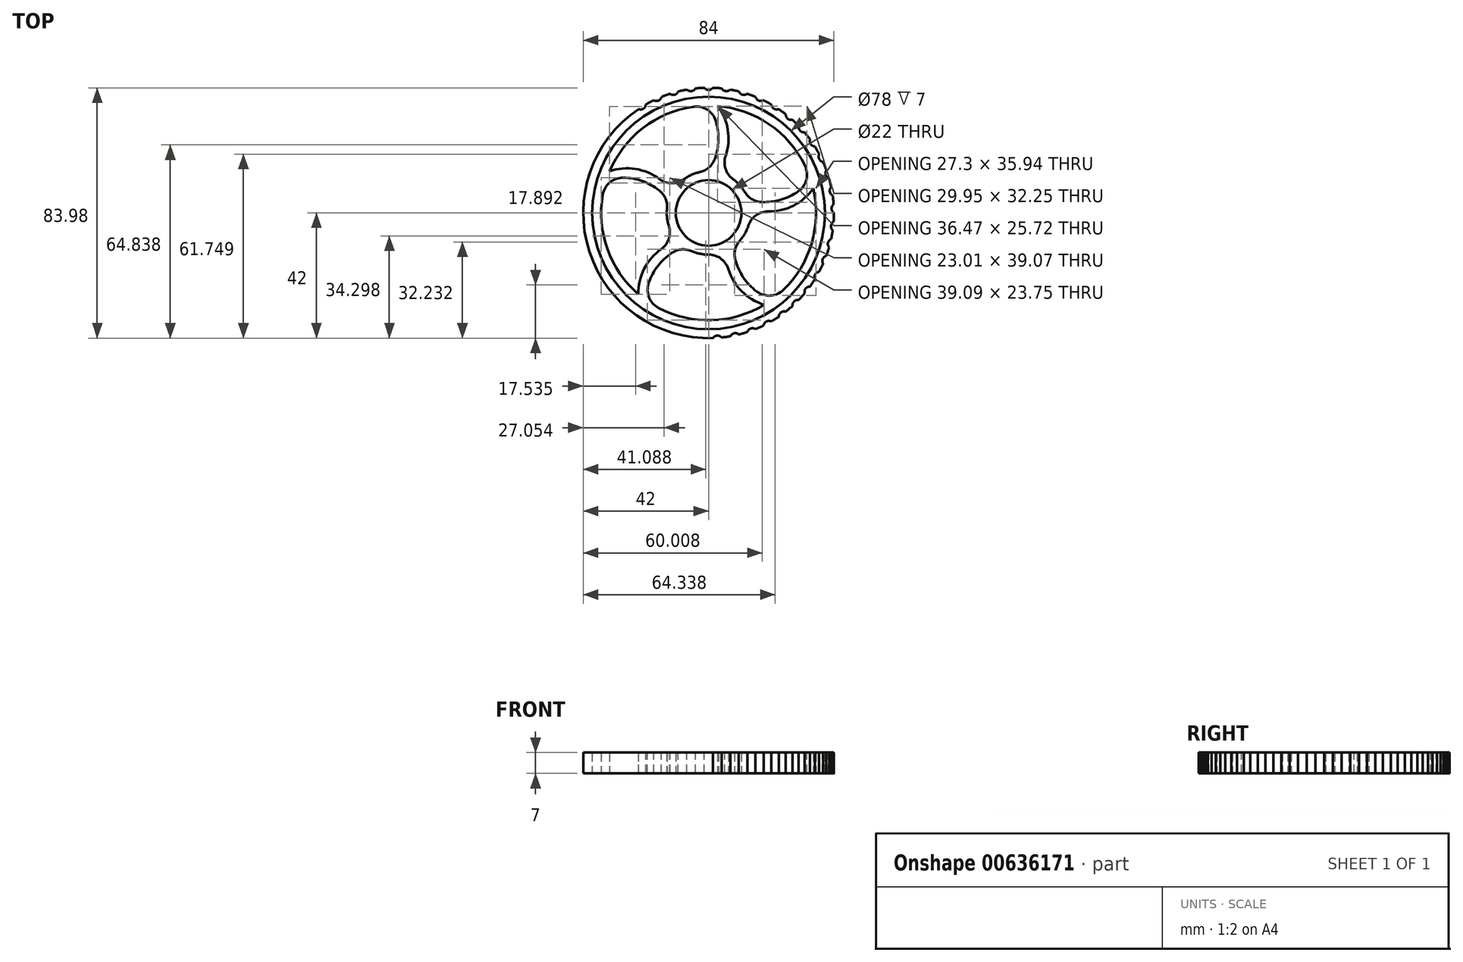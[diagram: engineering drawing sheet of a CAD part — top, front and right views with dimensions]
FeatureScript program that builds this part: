
annotation { "Feature Type Name" : "Feature", "Feature Type Description" : "" }
export const myFeature = defineFeature(function(context is Context, id is Id, definition is map)
    precondition{}
    {
        {
            var Q0;
            Q0=qCreatedBy(makeId("Top.planeOp"),FACE);
            var sketch = newSketch(context, id + "F0", { "sketchPlane" : qUnion([Q0])});
            skCircle(sketch, "E0", {"center": v(0, 0) * mm, "radius": 11 * mm});
            skCircle(sketch, "E1", {"center": v(0, 0) * mm, "radius": 14 * mm});
            skCircle(sketch, "E2", {"center": v(0, 0) * mm, "radius": 39 * mm});
            skCircle(sketch, "E3", {"center": v(0, 0) * mm, "radius": 36 * mm});
            skArc(sketch, "E4", {"start": v(0, 14) * mm, "mid": v(3.3, 25) * mm, "end": v(0, 36) * mm});
            skArc(sketch, "E5", {"start": v(2.72, 13.73) * mm, "mid": v(6.68, 24.75) * mm, "end": v(3.03, 35.87) * mm});
            skPoint(sketch, "E6.orphan", {"position": v(0, 39) * mm});
            skPoint(sketch, "E7.orphan", {"position": v(0, 11) * mm});
            skArc(sketch, "E8.1.0", {"start": v(-13.31, 4.33) * mm, "mid": v(-22.76, 10.86) * mm, "end": v(-34.24, 11.12) * mm});
            skArc(sketch, "E8.1.1", {"start": v(-12.22, 6.83) * mm, "mid": v(-21.47, 14) * mm, "end": v(-33.18, 13.97) * mm});
            skArc(sketch, "E8.2.0", {"start": v(-8.23, -11.33) * mm, "mid": v(-17.36, -18.29) * mm, "end": v(-21.16, -29.12) * mm});
            skArc(sketch, "E8.2.1", {"start": v(-10.28, -9.5) * mm, "mid": v(-19.96, -16.1) * mm, "end": v(-23.54, -27.24) * mm});
            skArc(sketch, "E9.1.3.0", {"start": v(8.23, -11.33) * mm, "mid": v(12.03, -22.16) * mm, "end": v(21.16, -29.12) * mm});
            skArc(sketch, "E9.4.3.0", {"start": v(5.87, -12.71) * mm, "mid": v(9.14, -23.95) * mm, "end": v(18.63, -30.8) * mm});
            skArc(sketch, "E9.1.4.0", {"start": v(13.31, 4.33) * mm, "mid": v(24.8, 4.6) * mm, "end": v(34.24, 11.12) * mm});
            skArc(sketch, "E9.4.4.0", {"start": v(13.9, 1.65) * mm, "mid": v(25.6, 1.3) * mm, "end": v(35.05, 8.2) * mm});
            skCircle(sketch, "E10", {"center": v(0, 0) * mm, "radius": 42 * mm});
            skSolve(sketch);
        }
        {
            var Q0;
            Q0=makeQuery(id+"F0.imprint","IMPRINT",FACE,{"disambiguationData":[TD([[makeQuery(id+"F0.imprint","IMPRINT",EDGE,{"derivedFrom":sQuery(id+"F0.wireOp",EDGE,"E0")}),-1.0]])]});
            var Q1;
            {var subQ0=sQuery(id+"F0.wireOp",EDGE,"E8.1.0");Q1=makeQuery(id+"F0.imprint","IMPRINT",FACE,{"disambiguationData":[TD([[makeQuery(id+"F0.imprint","IMPRINT",EDGE,{"derivedFrom":subQ0}),-1.0]])]});}
            var Q2;
            {var subQ0=sQuery(id+"F0.wireOp",EDGE,"E4");Q2=makeQuery(id+"F0.imprint","IMPRINT",FACE,{"disambiguationData":[TD([[makeQuery(id+"F0.imprint","IMPRINT",EDGE,{"derivedFrom":subQ0}),-1.0]])]});}
            var Q3;
            {var subQ0=sQuery(id+"F0.wireOp",EDGE,"E9.1.4.0");Q3=makeQuery(id+"F0.imprint","IMPRINT",FACE,{"disambiguationData":[TD([[makeQuery(id+"F0.imprint","IMPRINT",EDGE,{"derivedFrom":subQ0}),-1.0]])]});}
            var Q4;
            {var subQ0=sQuery(id+"F0.wireOp",EDGE,"E9.1.3.0");Q4=makeQuery(id+"F0.imprint","IMPRINT",FACE,{"disambiguationData":[TD([[makeQuery(id+"F0.imprint","IMPRINT",EDGE,{"derivedFrom":subQ0}),-1.0]])]});}
            var Q5;
            {var subQ0=sQuery(id+"F0.wireOp",EDGE,"E8.2.0");Q5=makeQuery(id+"F0.imprint","IMPRINT",FACE,{"disambiguationData":[TD([[makeQuery(id+"F0.imprint","IMPRINT",EDGE,{"derivedFrom":subQ0}),-1.0]])]});}
            var Q6;
            Q6=makeQuery(id+"F0.imprint","IMPRINT",FACE,{"disambiguationData":[TD([[makeQuery(id+"F0.imprint","IMPRINT",EDGE,{"derivedFrom":sQuery(id+"F0.wireOp",EDGE,"E2")}),1.0]])]});
            extrude(context, id + "F1", {"entities" : qUnion([Q0, Q1, Q2, Q3, Q4, Q5, Q6]), "endBound" : BoundingType.SYMMETRIC, "depth" : 7 * mm, "offsetDistance" : 25 * mm});
        }
        {
            var Q0;
            Q0=makeQuery(id+"F1.opExtrude","SWEPT_EDGE",EDGE,{"disambiguationData":[OSD([sQuery(id+"F0.wireOp",EDGE,"E1"),sQuery(id+"F0.wireOp",EDGE,"E8.1.1")])]});
            var Q1;
            Q1=makeQuery(id+"F1.opExtrude","SWEPT_EDGE",EDGE,{"disambiguationData":[OSD([sQuery(id+"F0.wireOp",EDGE,"E1"),sQuery(id+"F0.wireOp",EDGE,"E4")])]});
            var Q2;
            Q2=makeQuery(id+"F1.opExtrude","SWEPT_EDGE",EDGE,{"disambiguationData":[OSD([sQuery(id+"F0.wireOp",EDGE,"E1"),sQuery(id+"F0.wireOp",EDGE,"E5")])]});
            var Q3;
            Q3=makeQuery(id+"F1.opExtrude","SWEPT_EDGE",EDGE,{"disambiguationData":[OSD([sQuery(id+"F0.wireOp",EDGE,"E1"),sQuery(id+"F0.wireOp",EDGE,"E9.1.4.0")])]});
            var Q4;
            Q4=makeQuery(id+"F1.opExtrude","SWEPT_EDGE",EDGE,{"disambiguationData":[OSD([sQuery(id+"F0.wireOp",EDGE,"E1"),sQuery(id+"F0.wireOp",EDGE,"E9.4.4.0")])]});
            var Q5;
            Q5=makeQuery(id+"F1.opExtrude","SWEPT_EDGE",EDGE,{"disambiguationData":[OSD([sQuery(id+"F0.wireOp",EDGE,"E1"),sQuery(id+"F0.wireOp",EDGE,"E9.1.3.0")])]});
            var Q6;
            Q6=makeQuery(id+"F1.opExtrude","SWEPT_EDGE",EDGE,{"disambiguationData":[OSD([sQuery(id+"F0.wireOp",EDGE,"E1"),sQuery(id+"F0.wireOp",EDGE,"E8.2.0")])]});
            var Q7;
            Q7=makeQuery(id+"F1.opExtrude","SWEPT_EDGE",EDGE,{"disambiguationData":[OSD([sQuery(id+"F0.wireOp",EDGE,"E1"),sQuery(id+"F0.wireOp",EDGE,"E9.4.3.0")])]});
            var Q8;
            Q8=makeQuery(id+"F1.opExtrude","SWEPT_EDGE",EDGE,{"disambiguationData":[OSD([sQuery(id+"F0.wireOp",EDGE,"E1"),sQuery(id+"F0.wireOp",EDGE,"E8.1.0")])]});
            var Q9;
            Q9=makeQuery(id+"F1.opExtrude","SWEPT_EDGE",EDGE,{"disambiguationData":[OSD([sQuery(id+"F0.wireOp",EDGE,"E1"),sQuery(id+"F0.wireOp",EDGE,"E8.2.1")])]});
            var Q10;
            Q10=makeQuery(id+"F1.opExtrude","SWEPT_EDGE",EDGE,{"disambiguationData":[OSD([sQuery(id+"F0.wireOp",EDGE,"E3"),sQuery(id+"F0.wireOp",EDGE,"E9.1.4.0")])]});
            var Q11;
            Q11=makeQuery(id+"F1.opExtrude","SWEPT_EDGE",EDGE,{"disambiguationData":[OSD([sQuery(id+"F0.wireOp",EDGE,"E3"),sQuery(id+"F0.wireOp",EDGE,"E4")])]});
            var Q12;
            Q12=makeQuery(id+"F1.opExtrude","SWEPT_EDGE",EDGE,{"disambiguationData":[OSD([sQuery(id+"F0.wireOp",EDGE,"E3"),sQuery(id+"F0.wireOp",EDGE,"E8.1.0")])]});
            var Q13;
            Q13=makeQuery(id+"F1.opExtrude","SWEPT_EDGE",EDGE,{"disambiguationData":[OSD([sQuery(id+"F0.wireOp",EDGE,"E3"),sQuery(id+"F0.wireOp",EDGE,"E8.2.0")])]});
            var Q14;
            Q14=makeQuery(id+"F1.opExtrude","SWEPT_EDGE",EDGE,{"disambiguationData":[OSD([sQuery(id+"F0.wireOp",EDGE,"E3"),sQuery(id+"F0.wireOp",EDGE,"E9.1.3.0")])]});
            fillet(context, id + "F2", {"entities" : qUnion([Q0, Q1, Q2, Q3, Q4, Q5, Q6, Q7, Q8, Q9, Q10, Q11, Q12, Q13, Q14]), "radius" : 6.9 * mm, "tangentPropagation" : true, "allowEdgeOverflow" : false});
        }
        {
            var Q0;
            Q0=makeQuery(id+"F0.imprint","IMPRINT",FACE,{"disambiguationData":[TD([[makeQuery(id+"F0.imprint","IMPRINT",EDGE,{"derivedFrom":sQuery(id+"F0.wireOp",EDGE,"E2")}),-1.0]])]});
            extrude(context, id + "F3", {"entities" : qUnion([Q0]), "endBound" : BoundingType.SYMMETRIC, "depth" : 7 * mm, "offsetDistance" : 25 * mm});
        }
        {
            var Q0;
            Q0=makeQuery(id+"F3.opExtrude","CAP_FACE",FACE,{"disambiguationData":[OSD([sQuery(id+"F0.wireOp",EDGE,"E2"),sQuery(id+"F0.wireOp",EDGE,"E10")])],"isStart":false});
            var sketch = newSketch(context, id + "F4", { "sketchPlane" : qUnion([Q0])});
            skCircle(sketch, "E11", {"center": v(0, 0) * mm, "radius": 43 * mm});
            skCircle(sketch, "E12", {"center": v(0, 43) * mm, "radius": 1.75 * mm});
            skCircle(sketch, "E13.1.0", {"center": v(-5.98, 42.58) * mm, "radius": 1.75 * mm});
            skCircle(sketch, "E13.2.0", {"center": v(-11.85, 41.33) * mm, "radius": 1.75 * mm});
            skCircle(sketch, "E13.3.0", {"center": v(-17.49, 39.28) * mm, "radius": 1.75 * mm});
            skCircle(sketch, "E13.4.0", {"center": v(-22.79, 36.47) * mm, "radius": 1.75 * mm});
            skCircle(sketch, "E13.5.0", {"center": v(-27.64, 32.94) * mm, "radius": 1.75 * mm});
            skCircle(sketch, "E13.6.0", {"center": v(-31.96, 28.77) * mm, "radius": 1.75 * mm});
            skCircle(sketch, "E13.7.0", {"center": v(-35.65, 24.05) * mm, "radius": 1.75 * mm});
            skCircle(sketch, "E13.8.0", {"center": v(-38.65, 18.85) * mm, "radius": 1.75 * mm});
            skCircle(sketch, "E13.9.0", {"center": v(-40.9, 13.29) * mm, "radius": 1.75 * mm});
            skCircle(sketch, "E13.10.0", {"center": v(-42.35, 7.47) * mm, "radius": 1.75 * mm});
            skCircle(sketch, "E13.11.0", {"center": v(-42.97, 1.5) * mm, "radius": 1.75 * mm});
            skCircle(sketch, "E13.12.0", {"center": v(-42.76, -4.5) * mm, "radius": 1.75 * mm});
            skCircle(sketch, "E13.13.0", {"center": v(-41.72, -10.4) * mm, "radius": 1.75 * mm});
            skCircle(sketch, "E13.14.0", {"center": v(-39.87, -16.1) * mm, "radius": 1.75 * mm});
            skCircle(sketch, "E13.15.0", {"center": v(-37.24, -21.5) * mm, "radius": 1.75 * mm});
            skCircle(sketch, "E13.16.0", {"center": v(-33.88, -26.47) * mm, "radius": 1.75 * mm});
            skCircle(sketch, "E13.17.0", {"center": v(-29.87, -30.93) * mm, "radius": 1.75 * mm});
            skCircle(sketch, "E13.18.0", {"center": v(-25.27, -34.79) * mm, "radius": 1.75 * mm});
            skCircle(sketch, "E13.19.0", {"center": v(-20.19, -37.97) * mm, "radius": 1.75 * mm});
            skCircle(sketch, "E13.20.0", {"center": v(-14.7, -40.4) * mm, "radius": 1.75 * mm});
            skCircle(sketch, "E13.21.0", {"center": v(-8.94, -42.06) * mm, "radius": 1.75 * mm});
            skCircle(sketch, "E13.22.0", {"center": v(-3, -42.9) * mm, "radius": 1.75 * mm});
            skCircle(sketch, "E13.23.0", {"center": v(3, -42.9) * mm, "radius": 1.75 * mm});
            skCircle(sketch, "E13.24.0", {"center": v(8.94, -42.06) * mm, "radius": 1.75 * mm});
            skCircle(sketch, "E13.25.0", {"center": v(14.7, -40.4) * mm, "radius": 1.75 * mm});
            skCircle(sketch, "E13.26.0", {"center": v(20.19, -37.97) * mm, "radius": 1.75 * mm});
            skCircle(sketch, "E13.27.0", {"center": v(25.27, -34.79) * mm, "radius": 1.75 * mm});
            skCircle(sketch, "E13.28.0", {"center": v(29.87, -30.93) * mm, "radius": 1.75 * mm});
            skCircle(sketch, "E13.29.0", {"center": v(33.88, -26.47) * mm, "radius": 1.75 * mm});
            skCircle(sketch, "E13.30.0", {"center": v(37.24, -21.5) * mm, "radius": 1.75 * mm});
            skCircle(sketch, "E13.31.0", {"center": v(39.87, -16.1) * mm, "radius": 1.75 * mm});
            skCircle(sketch, "E13.32.0", {"center": v(41.72, -10.4) * mm, "radius": 1.75 * mm});
            skCircle(sketch, "E13.33.0", {"center": v(42.76, -4.5) * mm, "radius": 1.75 * mm});
            skCircle(sketch, "E13.34.0", {"center": v(42.97, 1.5) * mm, "radius": 1.75 * mm});
            skCircle(sketch, "E13.35.0", {"center": v(42.35, 7.47) * mm, "radius": 1.75 * mm});
            skCircle(sketch, "E13.36.0", {"center": v(40.9, 13.29) * mm, "radius": 1.75 * mm});
            skCircle(sketch, "E13.37.0", {"center": v(38.65, 18.85) * mm, "radius": 1.75 * mm});
            skCircle(sketch, "E13.38.0", {"center": v(35.65, 24.05) * mm, "radius": 1.75 * mm});
            skCircle(sketch, "E13.39.0", {"center": v(31.96, 28.77) * mm, "radius": 1.75 * mm});
            skCircle(sketch, "E13.40.0", {"center": v(27.64, 32.94) * mm, "radius": 1.75 * mm});
            skCircle(sketch, "E13.41.0", {"center": v(22.79, 36.47) * mm, "radius": 1.75 * mm});
            skCircle(sketch, "E13.42.0", {"center": v(17.49, 39.28) * mm, "radius": 1.75 * mm});
            skCircle(sketch, "E13.43.0", {"center": v(11.85, 41.33) * mm, "radius": 1.75 * mm});
            skCircle(sketch, "E13.44.0", {"center": v(5.98, 42.58) * mm, "radius": 1.75 * mm});
            skSolve(sketch);
        }
        {
            var Q0;
            {var subQ0=sQuery(id+"F4.wireOp",EDGE,"E13.35.0");var subQ1=sQuery(id+"F4.wireOp",EDGE,"E11");var subQ2=makeQuery(id+"F4.imprint","INTERSECT",VERTEX,{"disambiguationData":[OD(0.0)],"derivedFrom":[subQ1,subQ0]});Q0=makeQuery(id+"F4.imprint","IMPRINT",FACE,{"disambiguationData":[TD([[makeQuery(id+"F4.imprint","IMPRINT",EDGE,{"disambiguationData":[TD([[subQ2,-1.0]])],"derivedFrom":subQ1}),-1.0]])]});}
            var Q1;
            {var subQ0=sQuery(id+"F4.wireOp",EDGE,"E13.36.0");var subQ1=sQuery(id+"F4.wireOp",EDGE,"E11");var subQ2=makeQuery(id+"F4.imprint","INTERSECT",VERTEX,{"disambiguationData":[OD(0.0)],"derivedFrom":[subQ1,subQ0]});Q1=makeQuery(id+"F4.imprint","IMPRINT",FACE,{"disambiguationData":[TD([[makeQuery(id+"F4.imprint","IMPRINT",EDGE,{"disambiguationData":[TD([[subQ2,-1.0]])],"derivedFrom":subQ1}),-1.0]])]});}
            var Q2;
            {var subQ0=sQuery(id+"F4.wireOp",EDGE,"E13.37.0");var subQ1=sQuery(id+"F4.wireOp",EDGE,"E11");var subQ2=makeQuery(id+"F4.imprint","INTERSECT",VERTEX,{"disambiguationData":[OD(0.0)],"derivedFrom":[subQ1,subQ0]});Q2=makeQuery(id+"F4.imprint","IMPRINT",FACE,{"disambiguationData":[TD([[makeQuery(id+"F4.imprint","IMPRINT",EDGE,{"disambiguationData":[TD([[subQ2,-1.0]])],"derivedFrom":subQ1}),-1.0]])]});}
            var Q3;
            {var subQ0=sQuery(id+"F4.wireOp",EDGE,"E13.38.0");var subQ1=sQuery(id+"F4.wireOp",EDGE,"E11");var subQ2=makeQuery(id+"F4.imprint","INTERSECT",VERTEX,{"disambiguationData":[OD(0.0)],"derivedFrom":[subQ1,subQ0]});Q3=makeQuery(id+"F4.imprint","IMPRINT",FACE,{"disambiguationData":[TD([[makeQuery(id+"F4.imprint","IMPRINT",EDGE,{"disambiguationData":[TD([[subQ2,-1.0]])],"derivedFrom":subQ1}),-1.0]])]});}
            var Q4;
            {var subQ0=sQuery(id+"F4.wireOp",EDGE,"E13.39.0");var subQ1=sQuery(id+"F4.wireOp",EDGE,"E11");var subQ2=makeQuery(id+"F4.imprint","INTERSECT",VERTEX,{"disambiguationData":[OD(0.0)],"derivedFrom":[subQ1,subQ0]});Q4=makeQuery(id+"F4.imprint","IMPRINT",FACE,{"disambiguationData":[TD([[makeQuery(id+"F4.imprint","IMPRINT",EDGE,{"disambiguationData":[TD([[subQ2,-1.0]])],"derivedFrom":subQ1}),-1.0]])]});}
            var Q5;
            {var subQ0=sQuery(id+"F4.wireOp",EDGE,"E13.40.0");var subQ1=sQuery(id+"F4.wireOp",EDGE,"E11");var subQ2=makeQuery(id+"F4.imprint","INTERSECT",VERTEX,{"disambiguationData":[OD(0.0)],"derivedFrom":[subQ1,subQ0]});Q5=makeQuery(id+"F4.imprint","IMPRINT",FACE,{"disambiguationData":[TD([[makeQuery(id+"F4.imprint","IMPRINT",EDGE,{"disambiguationData":[TD([[subQ2,-1.0]])],"derivedFrom":subQ1}),-1.0]])]});}
            var Q6;
            {var subQ0=sQuery(id+"F4.wireOp",EDGE,"E13.41.0");var subQ1=sQuery(id+"F4.wireOp",EDGE,"E11");var subQ2=makeQuery(id+"F4.imprint","INTERSECT",VERTEX,{"disambiguationData":[OD(0.0)],"derivedFrom":[subQ1,subQ0]});Q6=makeQuery(id+"F4.imprint","IMPRINT",FACE,{"disambiguationData":[TD([[makeQuery(id+"F4.imprint","IMPRINT",EDGE,{"disambiguationData":[TD([[subQ2,-1.0]])],"derivedFrom":subQ1}),-1.0]])]});}
            var Q7;
            {var subQ0=sQuery(id+"F4.wireOp",EDGE,"E13.42.0");var subQ1=sQuery(id+"F4.wireOp",EDGE,"E11");var subQ2=makeQuery(id+"F4.imprint","INTERSECT",VERTEX,{"disambiguationData":[OD(0.0)],"derivedFrom":[subQ1,subQ0]});Q7=makeQuery(id+"F4.imprint","IMPRINT",FACE,{"disambiguationData":[TD([[makeQuery(id+"F4.imprint","IMPRINT",EDGE,{"disambiguationData":[TD([[subQ2,-1.0]])],"derivedFrom":subQ1}),-1.0]])]});}
            var Q8;
            {var subQ0=sQuery(id+"F4.wireOp",EDGE,"E13.43.0");var subQ1=sQuery(id+"F4.wireOp",EDGE,"E11");var subQ2=makeQuery(id+"F4.imprint","INTERSECT",VERTEX,{"disambiguationData":[OD(0.0)],"derivedFrom":[subQ1,subQ0]});Q8=makeQuery(id+"F4.imprint","IMPRINT",FACE,{"disambiguationData":[TD([[makeQuery(id+"F4.imprint","IMPRINT",EDGE,{"disambiguationData":[TD([[subQ2,-1.0]])],"derivedFrom":subQ1}),-1.0]])]});}
            var Q9;
            {var subQ0=sQuery(id+"F4.wireOp",EDGE,"E13.44.0");var subQ1=sQuery(id+"F4.wireOp",EDGE,"E11");var subQ2=makeQuery(id+"F4.imprint","INTERSECT",VERTEX,{"disambiguationData":[OD(0.0)],"derivedFrom":[subQ1,subQ0]});Q9=makeQuery(id+"F4.imprint","IMPRINT",FACE,{"disambiguationData":[TD([[makeQuery(id+"F4.imprint","IMPRINT",EDGE,{"disambiguationData":[TD([[subQ2,-1.0]])],"derivedFrom":subQ1}),-1.0]])]});}
            var Q10;
            {var subQ0=sQuery(id+"F4.wireOp",EDGE,"E12");var subQ1=sQuery(id+"F4.wireOp",EDGE,"E11");var subQ2=makeQuery(id+"F4.imprint","INTERSECT",VERTEX,{"disambiguationData":[OD(0.0)],"derivedFrom":[subQ1,subQ0]});Q10=makeQuery(id+"F4.imprint","IMPRINT",FACE,{"disambiguationData":[TD([[makeQuery(id+"F4.imprint","IMPRINT",EDGE,{"disambiguationData":[TD([[subQ2,-1.0]])],"derivedFrom":subQ1}),-1.0]])]});}
            var Q11;
            {var subQ0=sQuery(id+"F4.wireOp",EDGE,"E13.1.0");var subQ1=sQuery(id+"F4.wireOp",EDGE,"E11");var subQ2=makeQuery(id+"F4.imprint","INTERSECT",VERTEX,{"disambiguationData":[OD(0.0)],"derivedFrom":[subQ1,subQ0]});Q11=makeQuery(id+"F4.imprint","IMPRINT",FACE,{"disambiguationData":[TD([[makeQuery(id+"F4.imprint","IMPRINT",EDGE,{"disambiguationData":[TD([[subQ2,-1.0]])],"derivedFrom":subQ1}),-1.0]])]});}
            var Q12;
            {var subQ0=sQuery(id+"F4.wireOp",EDGE,"E13.2.0");var subQ1=sQuery(id+"F4.wireOp",EDGE,"E11");var subQ2=makeQuery(id+"F4.imprint","INTERSECT",VERTEX,{"disambiguationData":[OD(0.0)],"derivedFrom":[subQ1,subQ0]});Q12=makeQuery(id+"F4.imprint","IMPRINT",FACE,{"disambiguationData":[TD([[makeQuery(id+"F4.imprint","IMPRINT",EDGE,{"disambiguationData":[TD([[subQ2,-1.0]])],"derivedFrom":subQ1}),-1.0]])]});}
            var Q13;
            {var subQ0=sQuery(id+"F4.wireOp",EDGE,"E13.3.0");var subQ1=sQuery(id+"F4.wireOp",EDGE,"E11");var subQ2=makeQuery(id+"F4.imprint","INTERSECT",VERTEX,{"disambiguationData":[OD(0.0)],"derivedFrom":[subQ1,subQ0]});Q13=makeQuery(id+"F4.imprint","IMPRINT",FACE,{"disambiguationData":[TD([[makeQuery(id+"F4.imprint","IMPRINT",EDGE,{"disambiguationData":[TD([[subQ2,-1.0]])],"derivedFrom":subQ1}),-1.0]])]});}
            var Q14;
            {var subQ0=sQuery(id+"F4.wireOp",EDGE,"E13.4.0");var subQ1=sQuery(id+"F4.wireOp",EDGE,"E11");var subQ2=makeQuery(id+"F4.imprint","INTERSECT",VERTEX,{"disambiguationData":[OD(0.0)],"derivedFrom":[subQ1,subQ0]});Q14=makeQuery(id+"F4.imprint","IMPRINT",FACE,{"disambiguationData":[TD([[makeQuery(id+"F4.imprint","IMPRINT",EDGE,{"disambiguationData":[TD([[subQ2,-1.0]])],"derivedFrom":subQ1}),-1.0]])]});}
            var Q15;
            {var subQ0=sQuery(id+"F4.wireOp",EDGE,"E13.5.0");var subQ1=sQuery(id+"F4.wireOp",EDGE,"E11");var subQ2=makeQuery(id+"F4.imprint","INTERSECT",VERTEX,{"disambiguationData":[OD(0.0)],"derivedFrom":[subQ1,subQ0]});Q15=makeQuery(id+"F4.imprint","IMPRINT",FACE,{"disambiguationData":[TD([[makeQuery(id+"F4.imprint","IMPRINT",EDGE,{"disambiguationData":[TD([[subQ2,-1.0]])],"derivedFrom":subQ1}),-1.0]])]});}
            var Q16;
            {var subQ0=sQuery(id+"F4.wireOp",EDGE,"E13.6.0");var subQ1=sQuery(id+"F4.wireOp",EDGE,"E11");var subQ2=makeQuery(id+"F4.imprint","INTERSECT",VERTEX,{"disambiguationData":[OD(0.0)],"derivedFrom":[subQ1,subQ0]});Q16=makeQuery(id+"F4.imprint","IMPRINT",FACE,{"disambiguationData":[TD([[makeQuery(id+"F4.imprint","IMPRINT",EDGE,{"disambiguationData":[TD([[subQ2,-1.0]])],"derivedFrom":subQ1}),-1.0]])]});}
            var Q17;
            {var subQ0=sQuery(id+"F4.wireOp",EDGE,"E13.7.0");var subQ1=sQuery(id+"F4.wireOp",EDGE,"E11");var subQ2=makeQuery(id+"F4.imprint","INTERSECT",VERTEX,{"disambiguationData":[OD(0.0)],"derivedFrom":[subQ1,subQ0]});Q17=makeQuery(id+"F4.imprint","IMPRINT",FACE,{"disambiguationData":[TD([[makeQuery(id+"F4.imprint","IMPRINT",EDGE,{"disambiguationData":[TD([[subQ2,-1.0]])],"derivedFrom":subQ1}),-1.0]])]});}
            var Q18;
            {var subQ0=sQuery(id+"F4.wireOp",EDGE,"E13.8.0");var subQ1=sQuery(id+"F4.wireOp",EDGE,"E11");var subQ2=makeQuery(id+"F4.imprint","INTERSECT",VERTEX,{"disambiguationData":[OD(0.0)],"derivedFrom":[subQ1,subQ0]});Q18=makeQuery(id+"F4.imprint","IMPRINT",FACE,{"disambiguationData":[TD([[makeQuery(id+"F4.imprint","IMPRINT",EDGE,{"disambiguationData":[TD([[subQ2,-1.0]])],"derivedFrom":subQ1}),-1.0]])]});}
            var Q19;
            {var subQ0=sQuery(id+"F4.wireOp",EDGE,"E13.9.0");var subQ1=sQuery(id+"F4.wireOp",EDGE,"E11");var subQ2=makeQuery(id+"F4.imprint","INTERSECT",VERTEX,{"disambiguationData":[OD(0.0)],"derivedFrom":[subQ1,subQ0]});Q19=makeQuery(id+"F4.imprint","IMPRINT",FACE,{"disambiguationData":[TD([[makeQuery(id+"F4.imprint","IMPRINT",EDGE,{"disambiguationData":[TD([[subQ2,-1.0]])],"derivedFrom":subQ1}),-1.0]])]});}
            var Q20;
            {var subQ0=sQuery(id+"F4.wireOp",EDGE,"E13.10.0");var subQ1=sQuery(id+"F4.wireOp",EDGE,"E11");var subQ2=makeQuery(id+"F4.imprint","INTERSECT",VERTEX,{"disambiguationData":[OD(0.0)],"derivedFrom":[subQ1,subQ0]});Q20=makeQuery(id+"F4.imprint","IMPRINT",FACE,{"disambiguationData":[TD([[makeQuery(id+"F4.imprint","IMPRINT",EDGE,{"disambiguationData":[TD([[subQ2,-1.0]])],"derivedFrom":subQ1}),-1.0]])]});}
            var Q21;
            {var subQ0=sQuery(id+"F4.wireOp",EDGE,"E13.11.0");var subQ1=sQuery(id+"F4.wireOp",EDGE,"E11");var subQ2=makeQuery(id+"F4.imprint","INTERSECT",VERTEX,{"disambiguationData":[OD(0.0)],"derivedFrom":[subQ1,subQ0]});Q21=makeQuery(id+"F4.imprint","IMPRINT",FACE,{"disambiguationData":[TD([[makeQuery(id+"F4.imprint","IMPRINT",EDGE,{"disambiguationData":[TD([[subQ2,-1.0]])],"derivedFrom":subQ1}),-1.0]])]});}
            var Q22;
            {var subQ0=sQuery(id+"F4.wireOp",EDGE,"E13.12.0");var subQ1=sQuery(id+"F4.wireOp",EDGE,"E11");var subQ2=makeQuery(id+"F4.imprint","INTERSECT",VERTEX,{"disambiguationData":[OD(0.0)],"derivedFrom":[subQ1,subQ0]});Q22=makeQuery(id+"F4.imprint","IMPRINT",FACE,{"disambiguationData":[TD([[makeQuery(id+"F4.imprint","IMPRINT",EDGE,{"disambiguationData":[TD([[subQ2,-1.0]])],"derivedFrom":subQ1}),-1.0]])]});}
            var Q23;
            {var subQ0=sQuery(id+"F4.wireOp",EDGE,"E13.13.0");var subQ1=sQuery(id+"F4.wireOp",EDGE,"E11");var subQ2=makeQuery(id+"F4.imprint","INTERSECT",VERTEX,{"disambiguationData":[OD(0.0)],"derivedFrom":[subQ1,subQ0]});Q23=makeQuery(id+"F4.imprint","IMPRINT",FACE,{"disambiguationData":[TD([[makeQuery(id+"F4.imprint","IMPRINT",EDGE,{"disambiguationData":[TD([[subQ2,-1.0]])],"derivedFrom":subQ1}),-1.0]])]});}
            var Q24;
            {var subQ0=sQuery(id+"F4.wireOp",EDGE,"E13.14.0");var subQ1=sQuery(id+"F4.wireOp",EDGE,"E11");var subQ2=makeQuery(id+"F4.imprint","INTERSECT",VERTEX,{"disambiguationData":[OD(0.0)],"derivedFrom":[subQ1,subQ0]});Q24=makeQuery(id+"F4.imprint","IMPRINT",FACE,{"disambiguationData":[TD([[makeQuery(id+"F4.imprint","IMPRINT",EDGE,{"disambiguationData":[TD([[subQ2,-1.0]])],"derivedFrom":subQ1}),-1.0]])]});}
            var Q25;
            {var subQ0=sQuery(id+"F4.wireOp",EDGE,"E13.15.0");var subQ1=sQuery(id+"F4.wireOp",EDGE,"E11");var subQ2=makeQuery(id+"F4.imprint","INTERSECT",VERTEX,{"disambiguationData":[OD(0.0)],"derivedFrom":[subQ1,subQ0]});Q25=makeQuery(id+"F4.imprint","IMPRINT",FACE,{"disambiguationData":[TD([[makeQuery(id+"F4.imprint","IMPRINT",EDGE,{"disambiguationData":[TD([[subQ2,-1.0]])],"derivedFrom":subQ1}),-1.0]])]});}
            var Q26;
            {var subQ0=sQuery(id+"F4.wireOp",EDGE,"E13.16.0");var subQ1=sQuery(id+"F4.wireOp",EDGE,"E11");var subQ2=makeQuery(id+"F4.imprint","INTERSECT",VERTEX,{"disambiguationData":[OD(0.0)],"derivedFrom":[subQ1,subQ0]});Q26=makeQuery(id+"F4.imprint","IMPRINT",FACE,{"disambiguationData":[TD([[makeQuery(id+"F4.imprint","IMPRINT",EDGE,{"disambiguationData":[TD([[subQ2,-1.0]])],"derivedFrom":subQ1}),-1.0]])]});}
            var Q27;
            {var subQ0=sQuery(id+"F4.wireOp",EDGE,"E13.17.0");var subQ1=sQuery(id+"F4.wireOp",EDGE,"E11");var subQ2=makeQuery(id+"F4.imprint","INTERSECT",VERTEX,{"disambiguationData":[OD(0.0)],"derivedFrom":[subQ1,subQ0]});Q27=makeQuery(id+"F4.imprint","IMPRINT",FACE,{"disambiguationData":[TD([[makeQuery(id+"F4.imprint","IMPRINT",EDGE,{"disambiguationData":[TD([[subQ2,-1.0]])],"derivedFrom":subQ1}),-1.0]])]});}
            var Q28;
            {var subQ0=sQuery(id+"F4.wireOp",EDGE,"E13.18.0");var subQ1=sQuery(id+"F4.wireOp",EDGE,"E11");var subQ2=makeQuery(id+"F4.imprint","INTERSECT",VERTEX,{"disambiguationData":[OD(0.0)],"derivedFrom":[subQ1,subQ0]});Q28=makeQuery(id+"F4.imprint","IMPRINT",FACE,{"disambiguationData":[TD([[makeQuery(id+"F4.imprint","IMPRINT",EDGE,{"disambiguationData":[TD([[subQ2,-1.0]])],"derivedFrom":subQ1}),-1.0]])]});}
            var Q29;
            {var subQ0=sQuery(id+"F4.wireOp",EDGE,"E13.19.0");var subQ1=sQuery(id+"F4.wireOp",EDGE,"E11");var subQ2=makeQuery(id+"F4.imprint","INTERSECT",VERTEX,{"disambiguationData":[OD(0.0)],"derivedFrom":[subQ1,subQ0]});Q29=makeQuery(id+"F4.imprint","IMPRINT",FACE,{"disambiguationData":[TD([[makeQuery(id+"F4.imprint","IMPRINT",EDGE,{"disambiguationData":[TD([[subQ2,-1.0]])],"derivedFrom":subQ1}),-1.0]])]});}
            var Q30;
            {var subQ0=sQuery(id+"F4.wireOp",EDGE,"E13.20.0");var subQ1=sQuery(id+"F4.wireOp",EDGE,"E11");var subQ2=makeQuery(id+"F4.imprint","INTERSECT",VERTEX,{"disambiguationData":[OD(0.0)],"derivedFrom":[subQ1,subQ0]});Q30=makeQuery(id+"F4.imprint","IMPRINT",FACE,{"disambiguationData":[TD([[makeQuery(id+"F4.imprint","IMPRINT",EDGE,{"disambiguationData":[TD([[subQ2,-1.0]])],"derivedFrom":subQ1}),-1.0]])]});}
            var Q31;
            {var subQ0=sQuery(id+"F4.wireOp",EDGE,"E13.21.0");var subQ1=sQuery(id+"F4.wireOp",EDGE,"E11");var subQ2=makeQuery(id+"F4.imprint","INTERSECT",VERTEX,{"disambiguationData":[OD(0.0)],"derivedFrom":[subQ1,subQ0]});Q31=makeQuery(id+"F4.imprint","IMPRINT",FACE,{"disambiguationData":[TD([[makeQuery(id+"F4.imprint","IMPRINT",EDGE,{"disambiguationData":[TD([[subQ2,-1.0]])],"derivedFrom":subQ1}),-1.0]])]});}
            var Q32;
            {var subQ0=sQuery(id+"F4.wireOp",EDGE,"E13.22.0");var subQ1=sQuery(id+"F4.wireOp",EDGE,"E11");var subQ2=makeQuery(id+"F4.imprint","INTERSECT",VERTEX,{"disambiguationData":[OD(0.0)],"derivedFrom":[subQ1,subQ0]});Q32=makeQuery(id+"F4.imprint","IMPRINT",FACE,{"disambiguationData":[TD([[makeQuery(id+"F4.imprint","IMPRINT",EDGE,{"disambiguationData":[TD([[subQ2,-1.0]])],"derivedFrom":subQ1}),-1.0]])]});}
            var Q33;
            {var subQ0=sQuery(id+"F4.wireOp",EDGE,"E13.23.0");var subQ1=sQuery(id+"F4.wireOp",EDGE,"E11");var subQ2=makeQuery(id+"F4.imprint","INTERSECT",VERTEX,{"disambiguationData":[OD(0.0)],"derivedFrom":[subQ1,subQ0]});Q33=makeQuery(id+"F4.imprint","IMPRINT",FACE,{"disambiguationData":[TD([[makeQuery(id+"F4.imprint","IMPRINT",EDGE,{"disambiguationData":[TD([[subQ2,-1.0]])],"derivedFrom":subQ1}),-1.0]])]});}
            var Q34;
            {var subQ0=sQuery(id+"F4.wireOp",EDGE,"E13.24.0");var subQ1=sQuery(id+"F4.wireOp",EDGE,"E11");var subQ2=makeQuery(id+"F4.imprint","INTERSECT",VERTEX,{"disambiguationData":[OD(0.0)],"derivedFrom":[subQ1,subQ0]});Q34=makeQuery(id+"F4.imprint","IMPRINT",FACE,{"disambiguationData":[TD([[makeQuery(id+"F4.imprint","IMPRINT",EDGE,{"disambiguationData":[TD([[subQ2,-1.0]])],"derivedFrom":subQ1}),-1.0]])]});}
            var Q35;
            {var subQ0=sQuery(id+"F4.wireOp",EDGE,"E13.25.0");var subQ1=sQuery(id+"F4.wireOp",EDGE,"E11");var subQ2=makeQuery(id+"F4.imprint","INTERSECT",VERTEX,{"disambiguationData":[OD(0.0)],"derivedFrom":[subQ1,subQ0]});Q35=makeQuery(id+"F4.imprint","IMPRINT",FACE,{"disambiguationData":[TD([[makeQuery(id+"F4.imprint","IMPRINT",EDGE,{"disambiguationData":[TD([[subQ2,-1.0]])],"derivedFrom":subQ1}),-1.0]])]});}
            var Q36;
            {var subQ0=sQuery(id+"F4.wireOp",EDGE,"E13.26.0");var subQ1=sQuery(id+"F4.wireOp",EDGE,"E11");var subQ2=makeQuery(id+"F4.imprint","INTERSECT",VERTEX,{"disambiguationData":[OD(0.0)],"derivedFrom":[subQ1,subQ0]});Q36=makeQuery(id+"F4.imprint","IMPRINT",FACE,{"disambiguationData":[TD([[makeQuery(id+"F4.imprint","IMPRINT",EDGE,{"disambiguationData":[TD([[subQ2,-1.0]])],"derivedFrom":subQ1}),-1.0]])]});}
            var Q37;
            {var subQ0=sQuery(id+"F4.wireOp",EDGE,"E13.27.0");var subQ1=sQuery(id+"F4.wireOp",EDGE,"E11");var subQ2=makeQuery(id+"F4.imprint","INTERSECT",VERTEX,{"disambiguationData":[OD(0.0)],"derivedFrom":[subQ1,subQ0]});Q37=makeQuery(id+"F4.imprint","IMPRINT",FACE,{"disambiguationData":[TD([[makeQuery(id+"F4.imprint","IMPRINT",EDGE,{"disambiguationData":[TD([[subQ2,-1.0]])],"derivedFrom":subQ1}),-1.0]])]});}
            var Q38;
            {var subQ0=sQuery(id+"F4.wireOp",EDGE,"E13.28.0");var subQ1=sQuery(id+"F4.wireOp",EDGE,"E11");var subQ2=makeQuery(id+"F4.imprint","INTERSECT",VERTEX,{"disambiguationData":[OD(0.0)],"derivedFrom":[subQ1,subQ0]});Q38=makeQuery(id+"F4.imprint","IMPRINT",FACE,{"disambiguationData":[TD([[makeQuery(id+"F4.imprint","IMPRINT",EDGE,{"disambiguationData":[TD([[subQ2,-1.0]])],"derivedFrom":subQ1}),-1.0]])]});}
            var Q39;
            {var subQ0=sQuery(id+"F4.wireOp",EDGE,"E13.29.0");var subQ1=sQuery(id+"F4.wireOp",EDGE,"E11");var subQ2=makeQuery(id+"F4.imprint","INTERSECT",VERTEX,{"disambiguationData":[OD(0.0)],"derivedFrom":[subQ1,subQ0]});Q39=makeQuery(id+"F4.imprint","IMPRINT",FACE,{"disambiguationData":[TD([[makeQuery(id+"F4.imprint","IMPRINT",EDGE,{"disambiguationData":[TD([[subQ2,-1.0]])],"derivedFrom":subQ1}),-1.0]])]});}
            var Q40;
            {var subQ0=sQuery(id+"F4.wireOp",EDGE,"E13.30.0");var subQ1=sQuery(id+"F4.wireOp",EDGE,"E11");var subQ2=makeQuery(id+"F4.imprint","INTERSECT",VERTEX,{"disambiguationData":[OD(0.0)],"derivedFrom":[subQ1,subQ0]});Q40=makeQuery(id+"F4.imprint","IMPRINT",FACE,{"disambiguationData":[TD([[makeQuery(id+"F4.imprint","IMPRINT",EDGE,{"disambiguationData":[TD([[subQ2,-1.0]])],"derivedFrom":subQ1}),-1.0]])]});}
            var Q41;
            {var subQ0=sQuery(id+"F4.wireOp",EDGE,"E13.31.0");var subQ1=sQuery(id+"F4.wireOp",EDGE,"E11");var subQ2=makeQuery(id+"F4.imprint","INTERSECT",VERTEX,{"disambiguationData":[OD(0.0)],"derivedFrom":[subQ1,subQ0]});Q41=makeQuery(id+"F4.imprint","IMPRINT",FACE,{"disambiguationData":[TD([[makeQuery(id+"F4.imprint","IMPRINT",EDGE,{"disambiguationData":[TD([[subQ2,-1.0]])],"derivedFrom":subQ1}),-1.0]])]});}
            var Q42;
            {var subQ0=sQuery(id+"F4.wireOp",EDGE,"E13.32.0");var subQ1=sQuery(id+"F4.wireOp",EDGE,"E11");var subQ2=makeQuery(id+"F4.imprint","INTERSECT",VERTEX,{"disambiguationData":[OD(0.0)],"derivedFrom":[subQ1,subQ0]});Q42=makeQuery(id+"F4.imprint","IMPRINT",FACE,{"disambiguationData":[TD([[makeQuery(id+"F4.imprint","IMPRINT",EDGE,{"disambiguationData":[TD([[subQ2,-1.0]])],"derivedFrom":subQ1}),-1.0]])]});}
            var Q43;
            {var subQ0=sQuery(id+"F4.wireOp",EDGE,"E13.33.0");var subQ1=sQuery(id+"F4.wireOp",EDGE,"E11");var subQ2=makeQuery(id+"F4.imprint","INTERSECT",VERTEX,{"disambiguationData":[OD(0.0)],"derivedFrom":[subQ1,subQ0]});Q43=makeQuery(id+"F4.imprint","IMPRINT",FACE,{"disambiguationData":[TD([[makeQuery(id+"F4.imprint","IMPRINT",EDGE,{"disambiguationData":[TD([[subQ2,-1.0]])],"derivedFrom":subQ1}),-1.0]])]});}
            var Q44;
            {var subQ0=sQuery(id+"F4.wireOp",EDGE,"E13.34.0");var subQ1=sQuery(id+"F4.wireOp",EDGE,"E11");var subQ2=makeQuery(id+"F4.imprint","INTERSECT",VERTEX,{"disambiguationData":[OD(0.0)],"derivedFrom":[subQ1,subQ0]});Q44=makeQuery(id+"F4.imprint","IMPRINT",FACE,{"disambiguationData":[TD([[makeQuery(id+"F4.imprint","IMPRINT",EDGE,{"disambiguationData":[TD([[subQ2,1.0]])],"derivedFrom":subQ1}),-1.0]])]});}
            var Q45;
            {var subQ0=sQuery(id+"F4.wireOp",EDGE,"E12");var subQ1=makeQuery(id+"F3.opExtrude","CAP_EDGE",EDGE,{"disambiguationData":[OSD([sQuery(id+"F0.wireOp",EDGE,"E10")])],"isStart":false});var subQ2=makeQuery(id+"F4.imprint","INTERSECT",VERTEX,{"disambiguationData":[OD(0.0)],"derivedFrom":[subQ1,subQ0]});Q45=makeQuery(id+"F4.imprint","IMPRINT",FACE,{"disambiguationData":[TD([[makeQuery(id+"F4.imprint","IMPRINT",EDGE,{"disambiguationData":[TD([[subQ2,-1.0]])],"derivedFrom":subQ0}),1.0]])]});}
            var Q46;
            {var subQ0=sQuery(id+"F4.wireOp",EDGE,"E13.1.0");var subQ1=makeQuery(id+"F3.opExtrude","CAP_EDGE",EDGE,{"disambiguationData":[OSD([sQuery(id+"F0.wireOp",EDGE,"E10")])],"isStart":false});var subQ2=makeQuery(id+"F4.imprint","INTERSECT",VERTEX,{"disambiguationData":[OD(0.0)],"derivedFrom":[subQ1,subQ0]});Q46=makeQuery(id+"F4.imprint","IMPRINT",FACE,{"disambiguationData":[TD([[makeQuery(id+"F4.imprint","IMPRINT",EDGE,{"disambiguationData":[TD([[subQ2,-1.0]])],"derivedFrom":subQ0}),1.0]])]});}
            var Q47;
            {var subQ0=sQuery(id+"F4.wireOp",EDGE,"E13.2.0");var subQ1=makeQuery(id+"F3.opExtrude","CAP_EDGE",EDGE,{"disambiguationData":[OSD([sQuery(id+"F0.wireOp",EDGE,"E10")])],"isStart":false});var subQ2=makeQuery(id+"F4.imprint","INTERSECT",VERTEX,{"disambiguationData":[OD(0.0)],"derivedFrom":[subQ1,subQ0]});Q47=makeQuery(id+"F4.imprint","IMPRINT",FACE,{"disambiguationData":[TD([[makeQuery(id+"F4.imprint","IMPRINT",EDGE,{"disambiguationData":[TD([[subQ2,-1.0]])],"derivedFrom":subQ0}),1.0]])]});}
            var Q48;
            {var subQ0=sQuery(id+"F4.wireOp",EDGE,"E13.3.0");var subQ1=makeQuery(id+"F3.opExtrude","CAP_EDGE",EDGE,{"disambiguationData":[OSD([sQuery(id+"F0.wireOp",EDGE,"E10")])],"isStart":false});var subQ2=makeQuery(id+"F4.imprint","INTERSECT",VERTEX,{"disambiguationData":[OD(0.0)],"derivedFrom":[subQ1,subQ0]});Q48=makeQuery(id+"F4.imprint","IMPRINT",FACE,{"disambiguationData":[TD([[makeQuery(id+"F4.imprint","IMPRINT",EDGE,{"disambiguationData":[TD([[subQ2,-1.0]])],"derivedFrom":subQ0}),1.0]])]});}
            var Q49;
            {var subQ0=sQuery(id+"F4.wireOp",EDGE,"E13.4.0");var subQ1=makeQuery(id+"F3.opExtrude","CAP_EDGE",EDGE,{"disambiguationData":[OSD([sQuery(id+"F0.wireOp",EDGE,"E10")])],"isStart":false});var subQ2=makeQuery(id+"F4.imprint","INTERSECT",VERTEX,{"disambiguationData":[OD(0.0)],"derivedFrom":[subQ1,subQ0]});Q49=makeQuery(id+"F4.imprint","IMPRINT",FACE,{"disambiguationData":[TD([[makeQuery(id+"F4.imprint","IMPRINT",EDGE,{"disambiguationData":[TD([[subQ2,-1.0]])],"derivedFrom":subQ0}),1.0]])]});}
            var Q50;
            {var subQ0=sQuery(id+"F4.wireOp",EDGE,"E13.5.0");var subQ1=makeQuery(id+"F3.opExtrude","CAP_EDGE",EDGE,{"disambiguationData":[OSD([sQuery(id+"F0.wireOp",EDGE,"E10")])],"isStart":false});var subQ2=makeQuery(id+"F4.imprint","INTERSECT",VERTEX,{"disambiguationData":[OD(0.0)],"derivedFrom":[subQ1,subQ0]});Q50=makeQuery(id+"F4.imprint","IMPRINT",FACE,{"disambiguationData":[TD([[makeQuery(id+"F4.imprint","IMPRINT",EDGE,{"disambiguationData":[TD([[subQ2,-1.0]])],"derivedFrom":subQ0}),1.0]])]});}
            var Q51;
            {var subQ0=sQuery(id+"F4.wireOp",EDGE,"E13.6.0");var subQ1=makeQuery(id+"F3.opExtrude","CAP_EDGE",EDGE,{"disambiguationData":[OSD([sQuery(id+"F0.wireOp",EDGE,"E10")])],"isStart":false});var subQ2=makeQuery(id+"F4.imprint","INTERSECT",VERTEX,{"disambiguationData":[OD(0.0)],"derivedFrom":[subQ1,subQ0]});Q51=makeQuery(id+"F4.imprint","IMPRINT",FACE,{"disambiguationData":[TD([[makeQuery(id+"F4.imprint","IMPRINT",EDGE,{"disambiguationData":[TD([[subQ2,-1.0]])],"derivedFrom":subQ0}),1.0]])]});}
            var Q52;
            {var subQ0=sQuery(id+"F4.wireOp",EDGE,"E13.7.0");var subQ1=makeQuery(id+"F3.opExtrude","CAP_EDGE",EDGE,{"disambiguationData":[OSD([sQuery(id+"F0.wireOp",EDGE,"E10")])],"isStart":false});var subQ2=makeQuery(id+"F4.imprint","INTERSECT",VERTEX,{"disambiguationData":[OD(0.0)],"derivedFrom":[subQ1,subQ0]});Q52=makeQuery(id+"F4.imprint","IMPRINT",FACE,{"disambiguationData":[TD([[makeQuery(id+"F4.imprint","IMPRINT",EDGE,{"disambiguationData":[TD([[subQ2,-1.0]])],"derivedFrom":subQ0}),1.0]])]});}
            var Q53;
            {var subQ0=sQuery(id+"F4.wireOp",EDGE,"E13.8.0");var subQ1=makeQuery(id+"F3.opExtrude","CAP_EDGE",EDGE,{"disambiguationData":[OSD([sQuery(id+"F0.wireOp",EDGE,"E10")])],"isStart":false});var subQ2=makeQuery(id+"F4.imprint","INTERSECT",VERTEX,{"disambiguationData":[OD(0.0)],"derivedFrom":[subQ1,subQ0]});Q53=makeQuery(id+"F4.imprint","IMPRINT",FACE,{"disambiguationData":[TD([[makeQuery(id+"F4.imprint","IMPRINT",EDGE,{"disambiguationData":[TD([[subQ2,-1.0]])],"derivedFrom":subQ0}),1.0]])]});}
            var Q54;
            {var subQ0=sQuery(id+"F4.wireOp",EDGE,"E13.9.0");var subQ1=makeQuery(id+"F3.opExtrude","CAP_EDGE",EDGE,{"disambiguationData":[OSD([sQuery(id+"F0.wireOp",EDGE,"E10")])],"isStart":false});var subQ2=makeQuery(id+"F4.imprint","INTERSECT",VERTEX,{"disambiguationData":[OD(0.0)],"derivedFrom":[subQ1,subQ0]});Q54=makeQuery(id+"F4.imprint","IMPRINT",FACE,{"disambiguationData":[TD([[makeQuery(id+"F4.imprint","IMPRINT",EDGE,{"disambiguationData":[TD([[subQ2,-1.0]])],"derivedFrom":subQ0}),1.0]])]});}
            var Q55;
            {var subQ0=sQuery(id+"F4.wireOp",EDGE,"E13.10.0");var subQ1=makeQuery(id+"F3.opExtrude","CAP_EDGE",EDGE,{"disambiguationData":[OSD([sQuery(id+"F0.wireOp",EDGE,"E10")])],"isStart":false});var subQ2=makeQuery(id+"F4.imprint","INTERSECT",VERTEX,{"disambiguationData":[OD(0.0)],"derivedFrom":[subQ1,subQ0]});Q55=makeQuery(id+"F4.imprint","IMPRINT",FACE,{"disambiguationData":[TD([[makeQuery(id+"F4.imprint","IMPRINT",EDGE,{"disambiguationData":[TD([[subQ2,-1.0]])],"derivedFrom":subQ0}),1.0]])]});}
            var Q56;
            {var subQ0=sQuery(id+"F4.wireOp",EDGE,"E13.11.0");var subQ1=makeQuery(id+"F3.opExtrude","CAP_EDGE",EDGE,{"disambiguationData":[OSD([sQuery(id+"F0.wireOp",EDGE,"E10")])],"isStart":false});var subQ2=makeQuery(id+"F4.imprint","INTERSECT",VERTEX,{"disambiguationData":[OD(0.0)],"derivedFrom":[subQ1,subQ0]});Q56=makeQuery(id+"F4.imprint","IMPRINT",FACE,{"disambiguationData":[TD([[makeQuery(id+"F4.imprint","IMPRINT",EDGE,{"disambiguationData":[TD([[subQ2,-1.0]])],"derivedFrom":subQ0}),1.0]])]});}
            var Q57;
            {var subQ0=sQuery(id+"F4.wireOp",EDGE,"E13.12.0");var subQ1=makeQuery(id+"F3.opExtrude","CAP_EDGE",EDGE,{"disambiguationData":[OSD([sQuery(id+"F0.wireOp",EDGE,"E10")])],"isStart":false});var subQ2=makeQuery(id+"F4.imprint","INTERSECT",VERTEX,{"disambiguationData":[OD(0.0)],"derivedFrom":[subQ1,subQ0]});Q57=makeQuery(id+"F4.imprint","IMPRINT",FACE,{"disambiguationData":[TD([[makeQuery(id+"F4.imprint","IMPRINT",EDGE,{"disambiguationData":[TD([[subQ2,-1.0]])],"derivedFrom":subQ0}),1.0]])]});}
            var Q58;
            {var subQ0=sQuery(id+"F4.wireOp",EDGE,"E13.13.0");var subQ1=makeQuery(id+"F3.opExtrude","CAP_EDGE",EDGE,{"disambiguationData":[OSD([sQuery(id+"F0.wireOp",EDGE,"E10")])],"isStart":false});var subQ2=makeQuery(id+"F4.imprint","INTERSECT",VERTEX,{"disambiguationData":[OD(0.0)],"derivedFrom":[subQ1,subQ0]});Q58=makeQuery(id+"F4.imprint","IMPRINT",FACE,{"disambiguationData":[TD([[makeQuery(id+"F4.imprint","IMPRINT",EDGE,{"disambiguationData":[TD([[subQ2,-1.0]])],"derivedFrom":subQ0}),1.0]])]});}
            var Q59;
            {var subQ0=sQuery(id+"F4.wireOp",EDGE,"E13.14.0");var subQ1=makeQuery(id+"F3.opExtrude","CAP_EDGE",EDGE,{"disambiguationData":[OSD([sQuery(id+"F0.wireOp",EDGE,"E10")])],"isStart":false});var subQ2=makeQuery(id+"F4.imprint","INTERSECT",VERTEX,{"disambiguationData":[OD(0.0)],"derivedFrom":[subQ1,subQ0]});Q59=makeQuery(id+"F4.imprint","IMPRINT",FACE,{"disambiguationData":[TD([[makeQuery(id+"F4.imprint","IMPRINT",EDGE,{"disambiguationData":[TD([[subQ2,-1.0]])],"derivedFrom":subQ0}),1.0]])]});}
            var Q60;
            {var subQ0=sQuery(id+"F4.wireOp",EDGE,"E13.15.0");var subQ1=makeQuery(id+"F3.opExtrude","CAP_EDGE",EDGE,{"disambiguationData":[OSD([sQuery(id+"F0.wireOp",EDGE,"E10")])],"isStart":false});var subQ2=makeQuery(id+"F4.imprint","INTERSECT",VERTEX,{"disambiguationData":[OD(0.0)],"derivedFrom":[subQ1,subQ0]});Q60=makeQuery(id+"F4.imprint","IMPRINT",FACE,{"disambiguationData":[TD([[makeQuery(id+"F4.imprint","IMPRINT",EDGE,{"disambiguationData":[TD([[subQ2,-1.0]])],"derivedFrom":subQ0}),1.0]])]});}
            var Q61;
            {var subQ0=sQuery(id+"F4.wireOp",EDGE,"E13.16.0");var subQ1=makeQuery(id+"F3.opExtrude","CAP_EDGE",EDGE,{"disambiguationData":[OSD([sQuery(id+"F0.wireOp",EDGE,"E10")])],"isStart":false});var subQ2=makeQuery(id+"F4.imprint","INTERSECT",VERTEX,{"disambiguationData":[OD(0.0)],"derivedFrom":[subQ1,subQ0]});Q61=makeQuery(id+"F4.imprint","IMPRINT",FACE,{"disambiguationData":[TD([[makeQuery(id+"F4.imprint","IMPRINT",EDGE,{"disambiguationData":[TD([[subQ2,-1.0]])],"derivedFrom":subQ0}),1.0]])]});}
            var Q62;
            {var subQ0=sQuery(id+"F4.wireOp",EDGE,"E13.17.0");var subQ1=makeQuery(id+"F3.opExtrude","CAP_EDGE",EDGE,{"disambiguationData":[OSD([sQuery(id+"F0.wireOp",EDGE,"E10")])],"isStart":false});var subQ2=makeQuery(id+"F4.imprint","INTERSECT",VERTEX,{"disambiguationData":[OD(0.0)],"derivedFrom":[subQ1,subQ0]});Q62=makeQuery(id+"F4.imprint","IMPRINT",FACE,{"disambiguationData":[TD([[makeQuery(id+"F4.imprint","IMPRINT",EDGE,{"disambiguationData":[TD([[subQ2,-1.0]])],"derivedFrom":subQ0}),1.0]])]});}
            var Q63;
            {var subQ0=sQuery(id+"F4.wireOp",EDGE,"E13.18.0");var subQ1=makeQuery(id+"F3.opExtrude","CAP_EDGE",EDGE,{"disambiguationData":[OSD([sQuery(id+"F0.wireOp",EDGE,"E10")])],"isStart":false});var subQ2=makeQuery(id+"F4.imprint","INTERSECT",VERTEX,{"disambiguationData":[OD(0.0)],"derivedFrom":[subQ1,subQ0]});Q63=makeQuery(id+"F4.imprint","IMPRINT",FACE,{"disambiguationData":[TD([[makeQuery(id+"F4.imprint","IMPRINT",EDGE,{"disambiguationData":[TD([[subQ2,-1.0]])],"derivedFrom":subQ0}),1.0]])]});}
            var Q64;
            {var subQ0=sQuery(id+"F4.wireOp",EDGE,"E13.19.0");var subQ1=makeQuery(id+"F3.opExtrude","CAP_EDGE",EDGE,{"disambiguationData":[OSD([sQuery(id+"F0.wireOp",EDGE,"E10")])],"isStart":false});var subQ2=makeQuery(id+"F4.imprint","INTERSECT",VERTEX,{"disambiguationData":[OD(0.0)],"derivedFrom":[subQ1,subQ0]});Q64=makeQuery(id+"F4.imprint","IMPRINT",FACE,{"disambiguationData":[TD([[makeQuery(id+"F4.imprint","IMPRINT",EDGE,{"disambiguationData":[TD([[subQ2,-1.0]])],"derivedFrom":subQ0}),1.0]])]});}
            var Q65;
            {var subQ0=sQuery(id+"F4.wireOp",EDGE,"E13.20.0");var subQ1=makeQuery(id+"F3.opExtrude","CAP_EDGE",EDGE,{"disambiguationData":[OSD([sQuery(id+"F0.wireOp",EDGE,"E10")])],"isStart":false});var subQ2=makeQuery(id+"F4.imprint","INTERSECT",VERTEX,{"disambiguationData":[OD(0.0)],"derivedFrom":[subQ1,subQ0]});Q65=makeQuery(id+"F4.imprint","IMPRINT",FACE,{"disambiguationData":[TD([[makeQuery(id+"F4.imprint","IMPRINT",EDGE,{"disambiguationData":[TD([[subQ2,-1.0]])],"derivedFrom":subQ0}),1.0]])]});}
            var Q66;
            {var subQ0=sQuery(id+"F4.wireOp",EDGE,"E13.21.0");var subQ1=makeQuery(id+"F3.opExtrude","CAP_EDGE",EDGE,{"disambiguationData":[OSD([sQuery(id+"F0.wireOp",EDGE,"E10")])],"isStart":false});var subQ2=makeQuery(id+"F4.imprint","INTERSECT",VERTEX,{"disambiguationData":[OD(0.0)],"derivedFrom":[subQ1,subQ0]});Q66=makeQuery(id+"F4.imprint","IMPRINT",FACE,{"disambiguationData":[TD([[makeQuery(id+"F4.imprint","IMPRINT",EDGE,{"disambiguationData":[TD([[subQ2,-1.0]])],"derivedFrom":subQ0}),1.0]])]});}
            var Q67;
            {var subQ0=sQuery(id+"F4.wireOp",EDGE,"E13.22.0");var subQ1=makeQuery(id+"F3.opExtrude","CAP_EDGE",EDGE,{"disambiguationData":[OSD([sQuery(id+"F0.wireOp",EDGE,"E10")])],"isStart":false});var subQ2=makeQuery(id+"F4.imprint","INTERSECT",VERTEX,{"disambiguationData":[OD(0.0)],"derivedFrom":[subQ1,subQ0]});Q67=makeQuery(id+"F4.imprint","IMPRINT",FACE,{"disambiguationData":[TD([[makeQuery(id+"F4.imprint","IMPRINT",EDGE,{"disambiguationData":[TD([[subQ2,-1.0]])],"derivedFrom":subQ0}),1.0]])]});}
            var Q68;
            {var subQ0=sQuery(id+"F4.wireOp",EDGE,"E13.23.0");var subQ1=makeQuery(id+"F3.opExtrude","CAP_EDGE",EDGE,{"disambiguationData":[OSD([sQuery(id+"F0.wireOp",EDGE,"E10")])],"isStart":false});var subQ2=makeQuery(id+"F4.imprint","INTERSECT",VERTEX,{"disambiguationData":[OD(0.0)],"derivedFrom":[subQ1,subQ0]});Q68=makeQuery(id+"F4.imprint","IMPRINT",FACE,{"disambiguationData":[TD([[makeQuery(id+"F4.imprint","IMPRINT",EDGE,{"disambiguationData":[TD([[subQ2,-1.0]])],"derivedFrom":subQ0}),1.0]])]});}
            var Q69;
            {var subQ0=sQuery(id+"F4.wireOp",EDGE,"E13.24.0");var subQ1=makeQuery(id+"F3.opExtrude","CAP_EDGE",EDGE,{"disambiguationData":[OSD([sQuery(id+"F0.wireOp",EDGE,"E10")])],"isStart":false});var subQ2=makeQuery(id+"F4.imprint","INTERSECT",VERTEX,{"disambiguationData":[OD(0.0)],"derivedFrom":[subQ1,subQ0]});Q69=makeQuery(id+"F4.imprint","IMPRINT",FACE,{"disambiguationData":[TD([[makeQuery(id+"F4.imprint","IMPRINT",EDGE,{"disambiguationData":[TD([[subQ2,-1.0]])],"derivedFrom":subQ0}),1.0]])]});}
            var Q70;
            {var subQ0=sQuery(id+"F4.wireOp",EDGE,"E13.25.0");var subQ1=makeQuery(id+"F3.opExtrude","CAP_EDGE",EDGE,{"disambiguationData":[OSD([sQuery(id+"F0.wireOp",EDGE,"E10")])],"isStart":false});var subQ2=makeQuery(id+"F4.imprint","INTERSECT",VERTEX,{"disambiguationData":[OD(0.0)],"derivedFrom":[subQ1,subQ0]});Q70=makeQuery(id+"F4.imprint","IMPRINT",FACE,{"disambiguationData":[TD([[makeQuery(id+"F4.imprint","IMPRINT",EDGE,{"disambiguationData":[TD([[subQ2,-1.0]])],"derivedFrom":subQ0}),1.0]])]});}
            var Q71;
            {var subQ0=sQuery(id+"F4.wireOp",EDGE,"E13.26.0");var subQ1=makeQuery(id+"F3.opExtrude","CAP_EDGE",EDGE,{"disambiguationData":[OSD([sQuery(id+"F0.wireOp",EDGE,"E10")])],"isStart":false});var subQ2=makeQuery(id+"F4.imprint","INTERSECT",VERTEX,{"disambiguationData":[OD(0.0)],"derivedFrom":[subQ1,subQ0]});Q71=makeQuery(id+"F4.imprint","IMPRINT",FACE,{"disambiguationData":[TD([[makeQuery(id+"F4.imprint","IMPRINT",EDGE,{"disambiguationData":[TD([[subQ2,-1.0]])],"derivedFrom":subQ0}),1.0]])]});}
            var Q72;
            {var subQ0=sQuery(id+"F4.wireOp",EDGE,"E13.27.0");var subQ1=makeQuery(id+"F3.opExtrude","CAP_EDGE",EDGE,{"disambiguationData":[OSD([sQuery(id+"F0.wireOp",EDGE,"E10")])],"isStart":false});var subQ2=makeQuery(id+"F4.imprint","INTERSECT",VERTEX,{"disambiguationData":[OD(0.0)],"derivedFrom":[subQ1,subQ0]});Q72=makeQuery(id+"F4.imprint","IMPRINT",FACE,{"disambiguationData":[TD([[makeQuery(id+"F4.imprint","IMPRINT",EDGE,{"disambiguationData":[TD([[subQ2,-1.0]])],"derivedFrom":subQ0}),1.0]])]});}
            var Q73;
            {var subQ0=sQuery(id+"F4.wireOp",EDGE,"E13.28.0");var subQ1=makeQuery(id+"F3.opExtrude","CAP_EDGE",EDGE,{"disambiguationData":[OSD([sQuery(id+"F0.wireOp",EDGE,"E10")])],"isStart":false});var subQ2=makeQuery(id+"F4.imprint","INTERSECT",VERTEX,{"disambiguationData":[OD(0.0)],"derivedFrom":[subQ1,subQ0]});Q73=makeQuery(id+"F4.imprint","IMPRINT",FACE,{"disambiguationData":[TD([[makeQuery(id+"F4.imprint","IMPRINT",EDGE,{"disambiguationData":[TD([[subQ2,-1.0]])],"derivedFrom":subQ0}),1.0]])]});}
            var Q74;
            {var subQ0=sQuery(id+"F4.wireOp",EDGE,"E13.29.0");var subQ1=makeQuery(id+"F3.opExtrude","CAP_EDGE",EDGE,{"disambiguationData":[OSD([sQuery(id+"F0.wireOp",EDGE,"E10")])],"isStart":false});var subQ2=makeQuery(id+"F4.imprint","INTERSECT",VERTEX,{"disambiguationData":[OD(0.0)],"derivedFrom":[subQ1,subQ0]});Q74=makeQuery(id+"F4.imprint","IMPRINT",FACE,{"disambiguationData":[TD([[makeQuery(id+"F4.imprint","IMPRINT",EDGE,{"disambiguationData":[TD([[subQ2,-1.0]])],"derivedFrom":subQ0}),1.0]])]});}
            var Q75;
            {var subQ0=sQuery(id+"F4.wireOp",EDGE,"E13.30.0");var subQ1=makeQuery(id+"F3.opExtrude","CAP_EDGE",EDGE,{"disambiguationData":[OSD([sQuery(id+"F0.wireOp",EDGE,"E10")])],"isStart":false});var subQ2=makeQuery(id+"F4.imprint","INTERSECT",VERTEX,{"disambiguationData":[OD(0.0)],"derivedFrom":[subQ1,subQ0]});Q75=makeQuery(id+"F4.imprint","IMPRINT",FACE,{"disambiguationData":[TD([[makeQuery(id+"F4.imprint","IMPRINT",EDGE,{"disambiguationData":[TD([[subQ2,-1.0]])],"derivedFrom":subQ0}),1.0]])]});}
            var Q76;
            {var subQ0=sQuery(id+"F4.wireOp",EDGE,"E13.31.0");var subQ1=makeQuery(id+"F3.opExtrude","CAP_EDGE",EDGE,{"disambiguationData":[OSD([sQuery(id+"F0.wireOp",EDGE,"E10")])],"isStart":false});var subQ2=makeQuery(id+"F4.imprint","INTERSECT",VERTEX,{"disambiguationData":[OD(0.0)],"derivedFrom":[subQ1,subQ0]});Q76=makeQuery(id+"F4.imprint","IMPRINT",FACE,{"disambiguationData":[TD([[makeQuery(id+"F4.imprint","IMPRINT",EDGE,{"disambiguationData":[TD([[subQ2,-1.0]])],"derivedFrom":subQ0}),1.0]])]});}
            var Q77;
            {var subQ0=sQuery(id+"F4.wireOp",EDGE,"E13.32.0");var subQ1=makeQuery(id+"F3.opExtrude","CAP_EDGE",EDGE,{"disambiguationData":[OSD([sQuery(id+"F0.wireOp",EDGE,"E10")])],"isStart":false});var subQ2=makeQuery(id+"F4.imprint","INTERSECT",VERTEX,{"disambiguationData":[OD(0.0)],"derivedFrom":[subQ1,subQ0]});Q77=makeQuery(id+"F4.imprint","IMPRINT",FACE,{"disambiguationData":[TD([[makeQuery(id+"F4.imprint","IMPRINT",EDGE,{"disambiguationData":[TD([[subQ2,-1.0]])],"derivedFrom":subQ0}),1.0]])]});}
            var Q78;
            {var subQ0=sQuery(id+"F4.wireOp",EDGE,"E13.33.0");var subQ1=makeQuery(id+"F3.opExtrude","CAP_EDGE",EDGE,{"disambiguationData":[OSD([sQuery(id+"F0.wireOp",EDGE,"E10")])],"isStart":false});var subQ2=makeQuery(id+"F4.imprint","INTERSECT",VERTEX,{"disambiguationData":[OD(0.0)],"derivedFrom":[subQ1,subQ0]});Q78=makeQuery(id+"F4.imprint","IMPRINT",FACE,{"disambiguationData":[TD([[makeQuery(id+"F4.imprint","IMPRINT",EDGE,{"disambiguationData":[TD([[subQ2,-1.0]])],"derivedFrom":subQ0}),1.0]])]});}
            var Q79;
            {var subQ0=sQuery(id+"F4.wireOp",EDGE,"E13.34.0");var subQ1=makeQuery(id+"F3.opExtrude","CAP_EDGE",EDGE,{"disambiguationData":[OSD([sQuery(id+"F0.wireOp",EDGE,"E10")])],"isStart":false});var subQ2=makeQuery(id+"F4.imprint","INTERSECT",VERTEX,{"disambiguationData":[OD(0.0)],"derivedFrom":[subQ1,subQ0]});Q79=makeQuery(id+"F4.imprint","IMPRINT",FACE,{"disambiguationData":[TD([[makeQuery(id+"F4.imprint","IMPRINT",EDGE,{"disambiguationData":[TD([[subQ2,-1.0]])],"derivedFrom":subQ0}),1.0]])]});}
            var Q80;
            {var subQ0=sQuery(id+"F4.wireOp",EDGE,"E13.35.0");var subQ1=makeQuery(id+"F3.opExtrude","CAP_EDGE",EDGE,{"disambiguationData":[OSD([sQuery(id+"F0.wireOp",EDGE,"E10")])],"isStart":false});var subQ2=makeQuery(id+"F4.imprint","INTERSECT",VERTEX,{"disambiguationData":[OD(0.0)],"derivedFrom":[subQ1,subQ0]});Q80=makeQuery(id+"F4.imprint","IMPRINT",FACE,{"disambiguationData":[TD([[makeQuery(id+"F4.imprint","IMPRINT",EDGE,{"disambiguationData":[TD([[subQ2,-1.0]])],"derivedFrom":subQ0}),1.0]])]});}
            var Q81;
            {var subQ0=sQuery(id+"F4.wireOp",EDGE,"E13.36.0");var subQ1=makeQuery(id+"F3.opExtrude","CAP_EDGE",EDGE,{"disambiguationData":[OSD([sQuery(id+"F0.wireOp",EDGE,"E10")])],"isStart":false});var subQ2=makeQuery(id+"F4.imprint","INTERSECT",VERTEX,{"disambiguationData":[OD(0.0)],"derivedFrom":[subQ1,subQ0]});Q81=makeQuery(id+"F4.imprint","IMPRINT",FACE,{"disambiguationData":[TD([[makeQuery(id+"F4.imprint","IMPRINT",EDGE,{"disambiguationData":[TD([[subQ2,-1.0]])],"derivedFrom":subQ0}),1.0]])]});}
            var Q82;
            {var subQ0=sQuery(id+"F4.wireOp",EDGE,"E13.37.0");var subQ1=makeQuery(id+"F3.opExtrude","CAP_EDGE",EDGE,{"disambiguationData":[OSD([sQuery(id+"F0.wireOp",EDGE,"E10")])],"isStart":false});var subQ2=makeQuery(id+"F4.imprint","INTERSECT",VERTEX,{"disambiguationData":[OD(0.0)],"derivedFrom":[subQ1,subQ0]});Q82=makeQuery(id+"F4.imprint","IMPRINT",FACE,{"disambiguationData":[TD([[makeQuery(id+"F4.imprint","IMPRINT",EDGE,{"disambiguationData":[TD([[subQ2,-1.0]])],"derivedFrom":subQ0}),1.0]])]});}
            var Q83;
            {var subQ0=sQuery(id+"F4.wireOp",EDGE,"E13.38.0");var subQ1=makeQuery(id+"F3.opExtrude","CAP_EDGE",EDGE,{"disambiguationData":[OSD([sQuery(id+"F0.wireOp",EDGE,"E10")])],"isStart":false});var subQ2=makeQuery(id+"F4.imprint","INTERSECT",VERTEX,{"disambiguationData":[OD(0.0)],"derivedFrom":[subQ1,subQ0]});Q83=makeQuery(id+"F4.imprint","IMPRINT",FACE,{"disambiguationData":[TD([[makeQuery(id+"F4.imprint","IMPRINT",EDGE,{"disambiguationData":[TD([[subQ2,-1.0]])],"derivedFrom":subQ0}),1.0]])]});}
            var Q84;
            {var subQ0=sQuery(id+"F4.wireOp",EDGE,"E13.39.0");var subQ1=makeQuery(id+"F3.opExtrude","CAP_EDGE",EDGE,{"disambiguationData":[OSD([sQuery(id+"F0.wireOp",EDGE,"E10")])],"isStart":false});var subQ2=makeQuery(id+"F4.imprint","INTERSECT",VERTEX,{"disambiguationData":[OD(0.0)],"derivedFrom":[subQ1,subQ0]});Q84=makeQuery(id+"F4.imprint","IMPRINT",FACE,{"disambiguationData":[TD([[makeQuery(id+"F4.imprint","IMPRINT",EDGE,{"disambiguationData":[TD([[subQ2,-1.0]])],"derivedFrom":subQ0}),1.0]])]});}
            var Q85;
            {var subQ0=sQuery(id+"F4.wireOp",EDGE,"E13.40.0");var subQ1=makeQuery(id+"F3.opExtrude","CAP_EDGE",EDGE,{"disambiguationData":[OSD([sQuery(id+"F0.wireOp",EDGE,"E10")])],"isStart":false});var subQ2=makeQuery(id+"F4.imprint","INTERSECT",VERTEX,{"disambiguationData":[OD(0.0)],"derivedFrom":[subQ1,subQ0]});Q85=makeQuery(id+"F4.imprint","IMPRINT",FACE,{"disambiguationData":[TD([[makeQuery(id+"F4.imprint","IMPRINT",EDGE,{"disambiguationData":[TD([[subQ2,-1.0]])],"derivedFrom":subQ0}),1.0]])]});}
            var Q86;
            {var subQ0=sQuery(id+"F4.wireOp",EDGE,"E13.41.0");var subQ1=makeQuery(id+"F3.opExtrude","CAP_EDGE",EDGE,{"disambiguationData":[OSD([sQuery(id+"F0.wireOp",EDGE,"E10")])],"isStart":false});var subQ2=makeQuery(id+"F4.imprint","INTERSECT",VERTEX,{"disambiguationData":[OD(0.0)],"derivedFrom":[subQ1,subQ0]});Q86=makeQuery(id+"F4.imprint","IMPRINT",FACE,{"disambiguationData":[TD([[makeQuery(id+"F4.imprint","IMPRINT",EDGE,{"disambiguationData":[TD([[subQ2,-1.0]])],"derivedFrom":subQ0}),1.0]])]});}
            var Q87;
            {var subQ0=sQuery(id+"F4.wireOp",EDGE,"E13.42.0");var subQ1=makeQuery(id+"F3.opExtrude","CAP_EDGE",EDGE,{"disambiguationData":[OSD([sQuery(id+"F0.wireOp",EDGE,"E10")])],"isStart":false});var subQ2=makeQuery(id+"F4.imprint","INTERSECT",VERTEX,{"disambiguationData":[OD(0.0)],"derivedFrom":[subQ1,subQ0]});Q87=makeQuery(id+"F4.imprint","IMPRINT",FACE,{"disambiguationData":[TD([[makeQuery(id+"F4.imprint","IMPRINT",EDGE,{"disambiguationData":[TD([[subQ2,-1.0]])],"derivedFrom":subQ0}),1.0]])]});}
            var Q88;
            {var subQ0=sQuery(id+"F4.wireOp",EDGE,"E13.43.0");var subQ1=makeQuery(id+"F3.opExtrude","CAP_EDGE",EDGE,{"disambiguationData":[OSD([sQuery(id+"F0.wireOp",EDGE,"E10")])],"isStart":false});var subQ2=makeQuery(id+"F4.imprint","INTERSECT",VERTEX,{"disambiguationData":[OD(0.0)],"derivedFrom":[subQ1,subQ0]});Q88=makeQuery(id+"F4.imprint","IMPRINT",FACE,{"disambiguationData":[TD([[makeQuery(id+"F4.imprint","IMPRINT",EDGE,{"disambiguationData":[TD([[subQ2,-1.0]])],"derivedFrom":subQ0}),1.0]])]});}
            var Q89;
            {var subQ0=sQuery(id+"F4.wireOp",EDGE,"E13.44.0");var subQ1=makeQuery(id+"F3.opExtrude","CAP_EDGE",EDGE,{"disambiguationData":[OSD([sQuery(id+"F0.wireOp",EDGE,"E10")])],"isStart":false});var subQ2=makeQuery(id+"F4.imprint","INTERSECT",VERTEX,{"disambiguationData":[OD(0.0)],"derivedFrom":[subQ1,subQ0]});Q89=makeQuery(id+"F4.imprint","IMPRINT",FACE,{"disambiguationData":[TD([[makeQuery(id+"F4.imprint","IMPRINT",EDGE,{"disambiguationData":[TD([[subQ2,-1.0]])],"derivedFrom":subQ0}),1.0]])]});}
            var Q90;
            {var subQ0=sQuery(id+"F4.wireOp",EDGE,"E13.35.0");var subQ1=sQuery(id+"F4.wireOp",EDGE,"E11");var subQ2=makeQuery(id+"F4.imprint","INTERSECT",VERTEX,{"disambiguationData":[OD(0.0)],"derivedFrom":[subQ1,subQ0]});Q90=makeQuery(id+"F4.imprint","IMPRINT",FACE,{"disambiguationData":[TD([[makeQuery(id+"F4.imprint","IMPRINT",EDGE,{"disambiguationData":[TD([[subQ2,1.0]])],"derivedFrom":subQ1}),1.0]])]});}
            var Q91;
            {var subQ0=sQuery(id+"F4.wireOp",EDGE,"E13.35.0");var subQ1=sQuery(id+"F4.wireOp",EDGE,"E11");var subQ2=makeQuery(id+"F4.imprint","INTERSECT",VERTEX,{"disambiguationData":[OD(1.0)],"derivedFrom":[subQ1,subQ0]});Q91=makeQuery(id+"F4.imprint","IMPRINT",FACE,{"disambiguationData":[TD([[makeQuery(id+"F4.imprint","IMPRINT",EDGE,{"disambiguationData":[TD([[subQ2,-1.0]])],"derivedFrom":subQ1}),1.0]])]});}
            var Q92;
            {var subQ0=sQuery(id+"F4.wireOp",EDGE,"E13.36.0");var subQ1=sQuery(id+"F4.wireOp",EDGE,"E11");var subQ2=makeQuery(id+"F4.imprint","INTERSECT",VERTEX,{"disambiguationData":[OD(1.0)],"derivedFrom":[subQ1,subQ0]});Q92=makeQuery(id+"F4.imprint","IMPRINT",FACE,{"disambiguationData":[TD([[makeQuery(id+"F4.imprint","IMPRINT",EDGE,{"disambiguationData":[TD([[subQ2,-1.0]])],"derivedFrom":subQ1}),1.0]])]});}
            var Q93;
            {var subQ0=sQuery(id+"F4.wireOp",EDGE,"E13.37.0");var subQ1=sQuery(id+"F4.wireOp",EDGE,"E11");var subQ2=makeQuery(id+"F4.imprint","INTERSECT",VERTEX,{"disambiguationData":[OD(1.0)],"derivedFrom":[subQ1,subQ0]});Q93=makeQuery(id+"F4.imprint","IMPRINT",FACE,{"disambiguationData":[TD([[makeQuery(id+"F4.imprint","IMPRINT",EDGE,{"disambiguationData":[TD([[subQ2,-1.0]])],"derivedFrom":subQ1}),1.0]])]});}
            var Q94;
            {var subQ0=sQuery(id+"F4.wireOp",EDGE,"E13.38.0");var subQ1=sQuery(id+"F4.wireOp",EDGE,"E11");var subQ2=makeQuery(id+"F4.imprint","INTERSECT",VERTEX,{"disambiguationData":[OD(1.0)],"derivedFrom":[subQ1,subQ0]});Q94=makeQuery(id+"F4.imprint","IMPRINT",FACE,{"disambiguationData":[TD([[makeQuery(id+"F4.imprint","IMPRINT",EDGE,{"disambiguationData":[TD([[subQ2,-1.0]])],"derivedFrom":subQ1}),1.0]])]});}
            var Q95;
            {var subQ0=sQuery(id+"F4.wireOp",EDGE,"E13.39.0");var subQ1=sQuery(id+"F4.wireOp",EDGE,"E11");var subQ2=makeQuery(id+"F4.imprint","INTERSECT",VERTEX,{"disambiguationData":[OD(1.0)],"derivedFrom":[subQ1,subQ0]});Q95=makeQuery(id+"F4.imprint","IMPRINT",FACE,{"disambiguationData":[TD([[makeQuery(id+"F4.imprint","IMPRINT",EDGE,{"disambiguationData":[TD([[subQ2,-1.0]])],"derivedFrom":subQ1}),1.0]])]});}
            var Q96;
            {var subQ0=sQuery(id+"F4.wireOp",EDGE,"E13.40.0");var subQ1=sQuery(id+"F4.wireOp",EDGE,"E11");var subQ2=makeQuery(id+"F4.imprint","INTERSECT",VERTEX,{"disambiguationData":[OD(1.0)],"derivedFrom":[subQ1,subQ0]});Q96=makeQuery(id+"F4.imprint","IMPRINT",FACE,{"disambiguationData":[TD([[makeQuery(id+"F4.imprint","IMPRINT",EDGE,{"disambiguationData":[TD([[subQ2,-1.0]])],"derivedFrom":subQ1}),1.0]])]});}
            var Q97;
            {var subQ0=sQuery(id+"F4.wireOp",EDGE,"E13.41.0");var subQ1=sQuery(id+"F4.wireOp",EDGE,"E11");var subQ2=makeQuery(id+"F4.imprint","INTERSECT",VERTEX,{"disambiguationData":[OD(1.0)],"derivedFrom":[subQ1,subQ0]});Q97=makeQuery(id+"F4.imprint","IMPRINT",FACE,{"disambiguationData":[TD([[makeQuery(id+"F4.imprint","IMPRINT",EDGE,{"disambiguationData":[TD([[subQ2,-1.0]])],"derivedFrom":subQ1}),1.0]])]});}
            var Q98;
            {var subQ0=sQuery(id+"F4.wireOp",EDGE,"E13.42.0");var subQ1=sQuery(id+"F4.wireOp",EDGE,"E11");var subQ2=makeQuery(id+"F4.imprint","INTERSECT",VERTEX,{"disambiguationData":[OD(1.0)],"derivedFrom":[subQ1,subQ0]});Q98=makeQuery(id+"F4.imprint","IMPRINT",FACE,{"disambiguationData":[TD([[makeQuery(id+"F4.imprint","IMPRINT",EDGE,{"disambiguationData":[TD([[subQ2,-1.0]])],"derivedFrom":subQ1}),1.0]])]});}
            var Q99;
            {var subQ0=sQuery(id+"F4.wireOp",EDGE,"E13.43.0");var subQ1=sQuery(id+"F4.wireOp",EDGE,"E11");var subQ2=makeQuery(id+"F4.imprint","INTERSECT",VERTEX,{"disambiguationData":[OD(1.0)],"derivedFrom":[subQ1,subQ0]});Q99=makeQuery(id+"F4.imprint","IMPRINT",FACE,{"disambiguationData":[TD([[makeQuery(id+"F4.imprint","IMPRINT",EDGE,{"disambiguationData":[TD([[subQ2,-1.0]])],"derivedFrom":subQ1}),1.0]])]});}
            var Q100;
            {var subQ0=sQuery(id+"F4.wireOp",EDGE,"E13.44.0");var subQ1=sQuery(id+"F4.wireOp",EDGE,"E11");var subQ2=makeQuery(id+"F4.imprint","INTERSECT",VERTEX,{"disambiguationData":[OD(1.0)],"derivedFrom":[subQ1,subQ0]});Q100=makeQuery(id+"F4.imprint","IMPRINT",FACE,{"disambiguationData":[TD([[makeQuery(id+"F4.imprint","IMPRINT",EDGE,{"disambiguationData":[TD([[subQ2,-1.0]])],"derivedFrom":subQ1}),1.0]])]});}
            var Q101;
            {var subQ0=sQuery(id+"F4.wireOp",EDGE,"E12");var subQ1=sQuery(id+"F4.wireOp",EDGE,"E11");var subQ2=makeQuery(id+"F4.imprint","INTERSECT",VERTEX,{"disambiguationData":[OD(1.0)],"derivedFrom":[subQ1,subQ0]});Q101=makeQuery(id+"F4.imprint","IMPRINT",FACE,{"disambiguationData":[TD([[makeQuery(id+"F4.imprint","IMPRINT",EDGE,{"disambiguationData":[TD([[subQ2,-1.0]])],"derivedFrom":subQ1}),1.0]])]});}
            var Q102;
            {var subQ0=sQuery(id+"F4.wireOp",EDGE,"E13.1.0");var subQ1=sQuery(id+"F4.wireOp",EDGE,"E11");var subQ2=makeQuery(id+"F4.imprint","INTERSECT",VERTEX,{"disambiguationData":[OD(1.0)],"derivedFrom":[subQ1,subQ0]});Q102=makeQuery(id+"F4.imprint","IMPRINT",FACE,{"disambiguationData":[TD([[makeQuery(id+"F4.imprint","IMPRINT",EDGE,{"disambiguationData":[TD([[subQ2,-1.0]])],"derivedFrom":subQ1}),1.0]])]});}
            var Q103;
            {var subQ0=sQuery(id+"F4.wireOp",EDGE,"E13.2.0");var subQ1=sQuery(id+"F4.wireOp",EDGE,"E11");var subQ2=makeQuery(id+"F4.imprint","INTERSECT",VERTEX,{"disambiguationData":[OD(1.0)],"derivedFrom":[subQ1,subQ0]});Q103=makeQuery(id+"F4.imprint","IMPRINT",FACE,{"disambiguationData":[TD([[makeQuery(id+"F4.imprint","IMPRINT",EDGE,{"disambiguationData":[TD([[subQ2,-1.0]])],"derivedFrom":subQ1}),1.0]])]});}
            var Q104;
            {var subQ0=sQuery(id+"F4.wireOp",EDGE,"E13.3.0");var subQ1=sQuery(id+"F4.wireOp",EDGE,"E11");var subQ2=makeQuery(id+"F4.imprint","INTERSECT",VERTEX,{"disambiguationData":[OD(1.0)],"derivedFrom":[subQ1,subQ0]});Q104=makeQuery(id+"F4.imprint","IMPRINT",FACE,{"disambiguationData":[TD([[makeQuery(id+"F4.imprint","IMPRINT",EDGE,{"disambiguationData":[TD([[subQ2,-1.0]])],"derivedFrom":subQ1}),1.0]])]});}
            var Q105;
            {var subQ0=sQuery(id+"F4.wireOp",EDGE,"E13.4.0");var subQ1=sQuery(id+"F4.wireOp",EDGE,"E11");var subQ2=makeQuery(id+"F4.imprint","INTERSECT",VERTEX,{"disambiguationData":[OD(1.0)],"derivedFrom":[subQ1,subQ0]});Q105=makeQuery(id+"F4.imprint","IMPRINT",FACE,{"disambiguationData":[TD([[makeQuery(id+"F4.imprint","IMPRINT",EDGE,{"disambiguationData":[TD([[subQ2,-1.0]])],"derivedFrom":subQ1}),1.0]])]});}
            var Q106;
            {var subQ0=sQuery(id+"F4.wireOp",EDGE,"E13.5.0");var subQ1=sQuery(id+"F4.wireOp",EDGE,"E11");var subQ2=makeQuery(id+"F4.imprint","INTERSECT",VERTEX,{"disambiguationData":[OD(1.0)],"derivedFrom":[subQ1,subQ0]});Q106=makeQuery(id+"F4.imprint","IMPRINT",FACE,{"disambiguationData":[TD([[makeQuery(id+"F4.imprint","IMPRINT",EDGE,{"disambiguationData":[TD([[subQ2,-1.0]])],"derivedFrom":subQ1}),1.0]])]});}
            var Q107;
            {var subQ0=sQuery(id+"F4.wireOp",EDGE,"E13.6.0");var subQ1=sQuery(id+"F4.wireOp",EDGE,"E11");var subQ2=makeQuery(id+"F4.imprint","INTERSECT",VERTEX,{"disambiguationData":[OD(1.0)],"derivedFrom":[subQ1,subQ0]});Q107=makeQuery(id+"F4.imprint","IMPRINT",FACE,{"disambiguationData":[TD([[makeQuery(id+"F4.imprint","IMPRINT",EDGE,{"disambiguationData":[TD([[subQ2,-1.0]])],"derivedFrom":subQ1}),1.0]])]});}
            var Q108;
            {var subQ0=sQuery(id+"F4.wireOp",EDGE,"E13.7.0");var subQ1=sQuery(id+"F4.wireOp",EDGE,"E11");var subQ2=makeQuery(id+"F4.imprint","INTERSECT",VERTEX,{"disambiguationData":[OD(1.0)],"derivedFrom":[subQ1,subQ0]});Q108=makeQuery(id+"F4.imprint","IMPRINT",FACE,{"disambiguationData":[TD([[makeQuery(id+"F4.imprint","IMPRINT",EDGE,{"disambiguationData":[TD([[subQ2,-1.0]])],"derivedFrom":subQ1}),1.0]])]});}
            var Q109;
            {var subQ0=sQuery(id+"F4.wireOp",EDGE,"E13.8.0");var subQ1=sQuery(id+"F4.wireOp",EDGE,"E11");var subQ2=makeQuery(id+"F4.imprint","INTERSECT",VERTEX,{"disambiguationData":[OD(1.0)],"derivedFrom":[subQ1,subQ0]});Q109=makeQuery(id+"F4.imprint","IMPRINT",FACE,{"disambiguationData":[TD([[makeQuery(id+"F4.imprint","IMPRINT",EDGE,{"disambiguationData":[TD([[subQ2,-1.0]])],"derivedFrom":subQ1}),1.0]])]});}
            var Q110;
            {var subQ0=sQuery(id+"F4.wireOp",EDGE,"E13.9.0");var subQ1=sQuery(id+"F4.wireOp",EDGE,"E11");var subQ2=makeQuery(id+"F4.imprint","INTERSECT",VERTEX,{"disambiguationData":[OD(1.0)],"derivedFrom":[subQ1,subQ0]});Q110=makeQuery(id+"F4.imprint","IMPRINT",FACE,{"disambiguationData":[TD([[makeQuery(id+"F4.imprint","IMPRINT",EDGE,{"disambiguationData":[TD([[subQ2,-1.0]])],"derivedFrom":subQ1}),1.0]])]});}
            var Q111;
            {var subQ0=sQuery(id+"F4.wireOp",EDGE,"E13.10.0");var subQ1=sQuery(id+"F4.wireOp",EDGE,"E11");var subQ2=makeQuery(id+"F4.imprint","INTERSECT",VERTEX,{"disambiguationData":[OD(1.0)],"derivedFrom":[subQ1,subQ0]});Q111=makeQuery(id+"F4.imprint","IMPRINT",FACE,{"disambiguationData":[TD([[makeQuery(id+"F4.imprint","IMPRINT",EDGE,{"disambiguationData":[TD([[subQ2,-1.0]])],"derivedFrom":subQ1}),1.0]])]});}
            var Q112;
            {var subQ0=sQuery(id+"F4.wireOp",EDGE,"E13.11.0");var subQ1=sQuery(id+"F4.wireOp",EDGE,"E11");var subQ2=makeQuery(id+"F4.imprint","INTERSECT",VERTEX,{"disambiguationData":[OD(1.0)],"derivedFrom":[subQ1,subQ0]});Q112=makeQuery(id+"F4.imprint","IMPRINT",FACE,{"disambiguationData":[TD([[makeQuery(id+"F4.imprint","IMPRINT",EDGE,{"disambiguationData":[TD([[subQ2,-1.0]])],"derivedFrom":subQ1}),1.0]])]});}
            var Q113;
            {var subQ0=sQuery(id+"F4.wireOp",EDGE,"E13.12.0");var subQ1=sQuery(id+"F4.wireOp",EDGE,"E11");var subQ2=makeQuery(id+"F4.imprint","INTERSECT",VERTEX,{"disambiguationData":[OD(1.0)],"derivedFrom":[subQ1,subQ0]});Q113=makeQuery(id+"F4.imprint","IMPRINT",FACE,{"disambiguationData":[TD([[makeQuery(id+"F4.imprint","IMPRINT",EDGE,{"disambiguationData":[TD([[subQ2,-1.0]])],"derivedFrom":subQ1}),1.0]])]});}
            var Q114;
            {var subQ0=sQuery(id+"F4.wireOp",EDGE,"E13.13.0");var subQ1=sQuery(id+"F4.wireOp",EDGE,"E11");var subQ2=makeQuery(id+"F4.imprint","INTERSECT",VERTEX,{"disambiguationData":[OD(1.0)],"derivedFrom":[subQ1,subQ0]});Q114=makeQuery(id+"F4.imprint","IMPRINT",FACE,{"disambiguationData":[TD([[makeQuery(id+"F4.imprint","IMPRINT",EDGE,{"disambiguationData":[TD([[subQ2,-1.0]])],"derivedFrom":subQ1}),1.0]])]});}
            var Q115;
            {var subQ0=sQuery(id+"F4.wireOp",EDGE,"E13.14.0");var subQ1=sQuery(id+"F4.wireOp",EDGE,"E11");var subQ2=makeQuery(id+"F4.imprint","INTERSECT",VERTEX,{"disambiguationData":[OD(1.0)],"derivedFrom":[subQ1,subQ0]});Q115=makeQuery(id+"F4.imprint","IMPRINT",FACE,{"disambiguationData":[TD([[makeQuery(id+"F4.imprint","IMPRINT",EDGE,{"disambiguationData":[TD([[subQ2,-1.0]])],"derivedFrom":subQ1}),1.0]])]});}
            var Q116;
            {var subQ0=sQuery(id+"F4.wireOp",EDGE,"E13.15.0");var subQ1=sQuery(id+"F4.wireOp",EDGE,"E11");var subQ2=makeQuery(id+"F4.imprint","INTERSECT",VERTEX,{"disambiguationData":[OD(1.0)],"derivedFrom":[subQ1,subQ0]});Q116=makeQuery(id+"F4.imprint","IMPRINT",FACE,{"disambiguationData":[TD([[makeQuery(id+"F4.imprint","IMPRINT",EDGE,{"disambiguationData":[TD([[subQ2,-1.0]])],"derivedFrom":subQ1}),1.0]])]});}
            var Q117;
            {var subQ0=sQuery(id+"F4.wireOp",EDGE,"E13.16.0");var subQ1=sQuery(id+"F4.wireOp",EDGE,"E11");var subQ2=makeQuery(id+"F4.imprint","INTERSECT",VERTEX,{"disambiguationData":[OD(1.0)],"derivedFrom":[subQ1,subQ0]});Q117=makeQuery(id+"F4.imprint","IMPRINT",FACE,{"disambiguationData":[TD([[makeQuery(id+"F4.imprint","IMPRINT",EDGE,{"disambiguationData":[TD([[subQ2,-1.0]])],"derivedFrom":subQ1}),1.0]])]});}
            var Q118;
            {var subQ0=sQuery(id+"F4.wireOp",EDGE,"E13.17.0");var subQ1=sQuery(id+"F4.wireOp",EDGE,"E11");var subQ2=makeQuery(id+"F4.imprint","INTERSECT",VERTEX,{"disambiguationData":[OD(1.0)],"derivedFrom":[subQ1,subQ0]});Q118=makeQuery(id+"F4.imprint","IMPRINT",FACE,{"disambiguationData":[TD([[makeQuery(id+"F4.imprint","IMPRINT",EDGE,{"disambiguationData":[TD([[subQ2,-1.0]])],"derivedFrom":subQ1}),1.0]])]});}
            var Q119;
            {var subQ0=sQuery(id+"F4.wireOp",EDGE,"E13.18.0");var subQ1=sQuery(id+"F4.wireOp",EDGE,"E11");var subQ2=makeQuery(id+"F4.imprint","INTERSECT",VERTEX,{"disambiguationData":[OD(1.0)],"derivedFrom":[subQ1,subQ0]});Q119=makeQuery(id+"F4.imprint","IMPRINT",FACE,{"disambiguationData":[TD([[makeQuery(id+"F4.imprint","IMPRINT",EDGE,{"disambiguationData":[TD([[subQ2,-1.0]])],"derivedFrom":subQ1}),1.0]])]});}
            var Q120;
            {var subQ0=sQuery(id+"F4.wireOp",EDGE,"E13.19.0");var subQ1=sQuery(id+"F4.wireOp",EDGE,"E11");var subQ2=makeQuery(id+"F4.imprint","INTERSECT",VERTEX,{"disambiguationData":[OD(1.0)],"derivedFrom":[subQ1,subQ0]});Q120=makeQuery(id+"F4.imprint","IMPRINT",FACE,{"disambiguationData":[TD([[makeQuery(id+"F4.imprint","IMPRINT",EDGE,{"disambiguationData":[TD([[subQ2,-1.0]])],"derivedFrom":subQ1}),1.0]])]});}
            var Q121;
            {var subQ0=sQuery(id+"F4.wireOp",EDGE,"E13.20.0");var subQ1=sQuery(id+"F4.wireOp",EDGE,"E11");var subQ2=makeQuery(id+"F4.imprint","INTERSECT",VERTEX,{"disambiguationData":[OD(1.0)],"derivedFrom":[subQ1,subQ0]});Q121=makeQuery(id+"F4.imprint","IMPRINT",FACE,{"disambiguationData":[TD([[makeQuery(id+"F4.imprint","IMPRINT",EDGE,{"disambiguationData":[TD([[subQ2,-1.0]])],"derivedFrom":subQ1}),1.0]])]});}
            var Q122;
            {var subQ0=sQuery(id+"F4.wireOp",EDGE,"E13.21.0");var subQ1=sQuery(id+"F4.wireOp",EDGE,"E11");var subQ2=makeQuery(id+"F4.imprint","INTERSECT",VERTEX,{"disambiguationData":[OD(1.0)],"derivedFrom":[subQ1,subQ0]});Q122=makeQuery(id+"F4.imprint","IMPRINT",FACE,{"disambiguationData":[TD([[makeQuery(id+"F4.imprint","IMPRINT",EDGE,{"disambiguationData":[TD([[subQ2,-1.0]])],"derivedFrom":subQ1}),1.0]])]});}
            var Q123;
            {var subQ0=sQuery(id+"F4.wireOp",EDGE,"E13.22.0");var subQ1=sQuery(id+"F4.wireOp",EDGE,"E11");var subQ2=makeQuery(id+"F4.imprint","INTERSECT",VERTEX,{"disambiguationData":[OD(1.0)],"derivedFrom":[subQ1,subQ0]});Q123=makeQuery(id+"F4.imprint","IMPRINT",FACE,{"disambiguationData":[TD([[makeQuery(id+"F4.imprint","IMPRINT",EDGE,{"disambiguationData":[TD([[subQ2,-1.0]])],"derivedFrom":subQ1}),1.0]])]});}
            var Q124;
            {var subQ0=sQuery(id+"F4.wireOp",EDGE,"E13.23.0");var subQ1=sQuery(id+"F4.wireOp",EDGE,"E11");var subQ2=makeQuery(id+"F4.imprint","INTERSECT",VERTEX,{"disambiguationData":[OD(1.0)],"derivedFrom":[subQ1,subQ0]});Q124=makeQuery(id+"F4.imprint","IMPRINT",FACE,{"disambiguationData":[TD([[makeQuery(id+"F4.imprint","IMPRINT",EDGE,{"disambiguationData":[TD([[subQ2,-1.0]])],"derivedFrom":subQ1}),1.0]])]});}
            var Q125;
            {var subQ0=sQuery(id+"F4.wireOp",EDGE,"E13.24.0");var subQ1=sQuery(id+"F4.wireOp",EDGE,"E11");var subQ2=makeQuery(id+"F4.imprint","INTERSECT",VERTEX,{"disambiguationData":[OD(1.0)],"derivedFrom":[subQ1,subQ0]});Q125=makeQuery(id+"F4.imprint","IMPRINT",FACE,{"disambiguationData":[TD([[makeQuery(id+"F4.imprint","IMPRINT",EDGE,{"disambiguationData":[TD([[subQ2,-1.0]])],"derivedFrom":subQ1}),1.0]])]});}
            var Q126;
            {var subQ0=sQuery(id+"F4.wireOp",EDGE,"E13.25.0");var subQ1=sQuery(id+"F4.wireOp",EDGE,"E11");var subQ2=makeQuery(id+"F4.imprint","INTERSECT",VERTEX,{"disambiguationData":[OD(1.0)],"derivedFrom":[subQ1,subQ0]});Q126=makeQuery(id+"F4.imprint","IMPRINT",FACE,{"disambiguationData":[TD([[makeQuery(id+"F4.imprint","IMPRINT",EDGE,{"disambiguationData":[TD([[subQ2,-1.0]])],"derivedFrom":subQ1}),1.0]])]});}
            var Q127;
            {var subQ0=sQuery(id+"F4.wireOp",EDGE,"E13.26.0");var subQ1=sQuery(id+"F4.wireOp",EDGE,"E11");var subQ2=makeQuery(id+"F4.imprint","INTERSECT",VERTEX,{"disambiguationData":[OD(1.0)],"derivedFrom":[subQ1,subQ0]});Q127=makeQuery(id+"F4.imprint","IMPRINT",FACE,{"disambiguationData":[TD([[makeQuery(id+"F4.imprint","IMPRINT",EDGE,{"disambiguationData":[TD([[subQ2,-1.0]])],"derivedFrom":subQ1}),1.0]])]});}
            var Q128;
            {var subQ0=sQuery(id+"F4.wireOp",EDGE,"E13.27.0");var subQ1=sQuery(id+"F4.wireOp",EDGE,"E11");var subQ2=makeQuery(id+"F4.imprint","INTERSECT",VERTEX,{"disambiguationData":[OD(1.0)],"derivedFrom":[subQ1,subQ0]});Q128=makeQuery(id+"F4.imprint","IMPRINT",FACE,{"disambiguationData":[TD([[makeQuery(id+"F4.imprint","IMPRINT",EDGE,{"disambiguationData":[TD([[subQ2,-1.0]])],"derivedFrom":subQ1}),1.0]])]});}
            var Q129;
            {var subQ0=sQuery(id+"F4.wireOp",EDGE,"E13.28.0");var subQ1=sQuery(id+"F4.wireOp",EDGE,"E11");var subQ2=makeQuery(id+"F4.imprint","INTERSECT",VERTEX,{"disambiguationData":[OD(1.0)],"derivedFrom":[subQ1,subQ0]});Q129=makeQuery(id+"F4.imprint","IMPRINT",FACE,{"disambiguationData":[TD([[makeQuery(id+"F4.imprint","IMPRINT",EDGE,{"disambiguationData":[TD([[subQ2,-1.0]])],"derivedFrom":subQ1}),1.0]])]});}
            var Q130;
            {var subQ0=sQuery(id+"F4.wireOp",EDGE,"E13.29.0");var subQ1=sQuery(id+"F4.wireOp",EDGE,"E11");var subQ2=makeQuery(id+"F4.imprint","INTERSECT",VERTEX,{"disambiguationData":[OD(1.0)],"derivedFrom":[subQ1,subQ0]});Q130=makeQuery(id+"F4.imprint","IMPRINT",FACE,{"disambiguationData":[TD([[makeQuery(id+"F4.imprint","IMPRINT",EDGE,{"disambiguationData":[TD([[subQ2,-1.0]])],"derivedFrom":subQ1}),1.0]])]});}
            var Q131;
            {var subQ0=sQuery(id+"F4.wireOp",EDGE,"E13.30.0");var subQ1=sQuery(id+"F4.wireOp",EDGE,"E11");var subQ2=makeQuery(id+"F4.imprint","INTERSECT",VERTEX,{"disambiguationData":[OD(1.0)],"derivedFrom":[subQ1,subQ0]});Q131=makeQuery(id+"F4.imprint","IMPRINT",FACE,{"disambiguationData":[TD([[makeQuery(id+"F4.imprint","IMPRINT",EDGE,{"disambiguationData":[TD([[subQ2,-1.0]])],"derivedFrom":subQ1}),1.0]])]});}
            var Q132;
            {var subQ0=sQuery(id+"F4.wireOp",EDGE,"E13.31.0");var subQ1=sQuery(id+"F4.wireOp",EDGE,"E11");var subQ2=makeQuery(id+"F4.imprint","INTERSECT",VERTEX,{"disambiguationData":[OD(1.0)],"derivedFrom":[subQ1,subQ0]});Q132=makeQuery(id+"F4.imprint","IMPRINT",FACE,{"disambiguationData":[TD([[makeQuery(id+"F4.imprint","IMPRINT",EDGE,{"disambiguationData":[TD([[subQ2,-1.0]])],"derivedFrom":subQ1}),1.0]])]});}
            var Q133;
            {var subQ0=sQuery(id+"F4.wireOp",EDGE,"E13.32.0");var subQ1=sQuery(id+"F4.wireOp",EDGE,"E11");var subQ2=makeQuery(id+"F4.imprint","INTERSECT",VERTEX,{"disambiguationData":[OD(1.0)],"derivedFrom":[subQ1,subQ0]});Q133=makeQuery(id+"F4.imprint","IMPRINT",FACE,{"disambiguationData":[TD([[makeQuery(id+"F4.imprint","IMPRINT",EDGE,{"disambiguationData":[TD([[subQ2,-1.0]])],"derivedFrom":subQ1}),1.0]])]});}
            var Q134;
            {var subQ0=sQuery(id+"F4.wireOp",EDGE,"E13.33.0");var subQ1=sQuery(id+"F4.wireOp",EDGE,"E11");var subQ2=makeQuery(id+"F4.imprint","INTERSECT",VERTEX,{"disambiguationData":[OD(1.0)],"derivedFrom":[subQ1,subQ0]});Q134=makeQuery(id+"F4.imprint","IMPRINT",FACE,{"disambiguationData":[TD([[makeQuery(id+"F4.imprint","IMPRINT",EDGE,{"disambiguationData":[TD([[subQ2,-1.0]])],"derivedFrom":subQ1}),1.0]])]});}
            var Q135;
            {var subQ0=sQuery(id+"F4.wireOp",EDGE,"E13.35.0");var subQ1=sQuery(id+"F4.wireOp",EDGE,"E11");var subQ2=makeQuery(id+"F4.imprint","INTERSECT",VERTEX,{"disambiguationData":[OD(0.0)],"derivedFrom":[subQ1,subQ0]});Q135=makeQuery(id+"F4.imprint","IMPRINT",FACE,{"disambiguationData":[TD([[makeQuery(id+"F4.imprint","IMPRINT",EDGE,{"disambiguationData":[TD([[subQ2,-1.0]])],"derivedFrom":subQ1}),1.0]])]});}
            var Q136;
            {var subQ0=sQuery(id+"F4.wireOp",EDGE,"E13.36.0");var subQ1=sQuery(id+"F4.wireOp",EDGE,"E11");var subQ2=makeQuery(id+"F4.imprint","INTERSECT",VERTEX,{"disambiguationData":[OD(0.0)],"derivedFrom":[subQ1,subQ0]});Q136=makeQuery(id+"F4.imprint","IMPRINT",FACE,{"disambiguationData":[TD([[makeQuery(id+"F4.imprint","IMPRINT",EDGE,{"disambiguationData":[TD([[subQ2,-1.0]])],"derivedFrom":subQ1}),1.0]])]});}
            var Q137;
            {var subQ0=sQuery(id+"F4.wireOp",EDGE,"E13.37.0");var subQ1=sQuery(id+"F4.wireOp",EDGE,"E11");var subQ2=makeQuery(id+"F4.imprint","INTERSECT",VERTEX,{"disambiguationData":[OD(0.0)],"derivedFrom":[subQ1,subQ0]});Q137=makeQuery(id+"F4.imprint","IMPRINT",FACE,{"disambiguationData":[TD([[makeQuery(id+"F4.imprint","IMPRINT",EDGE,{"disambiguationData":[TD([[subQ2,-1.0]])],"derivedFrom":subQ1}),1.0]])]});}
            var Q138;
            {var subQ0=sQuery(id+"F4.wireOp",EDGE,"E13.38.0");var subQ1=sQuery(id+"F4.wireOp",EDGE,"E11");var subQ2=makeQuery(id+"F4.imprint","INTERSECT",VERTEX,{"disambiguationData":[OD(0.0)],"derivedFrom":[subQ1,subQ0]});Q138=makeQuery(id+"F4.imprint","IMPRINT",FACE,{"disambiguationData":[TD([[makeQuery(id+"F4.imprint","IMPRINT",EDGE,{"disambiguationData":[TD([[subQ2,-1.0]])],"derivedFrom":subQ1}),1.0]])]});}
            var Q139;
            {var subQ0=sQuery(id+"F4.wireOp",EDGE,"E13.39.0");var subQ1=sQuery(id+"F4.wireOp",EDGE,"E11");var subQ2=makeQuery(id+"F4.imprint","INTERSECT",VERTEX,{"disambiguationData":[OD(0.0)],"derivedFrom":[subQ1,subQ0]});Q139=makeQuery(id+"F4.imprint","IMPRINT",FACE,{"disambiguationData":[TD([[makeQuery(id+"F4.imprint","IMPRINT",EDGE,{"disambiguationData":[TD([[subQ2,-1.0]])],"derivedFrom":subQ1}),1.0]])]});}
            var Q140;
            {var subQ0=sQuery(id+"F4.wireOp",EDGE,"E13.40.0");var subQ1=sQuery(id+"F4.wireOp",EDGE,"E11");var subQ2=makeQuery(id+"F4.imprint","INTERSECT",VERTEX,{"disambiguationData":[OD(0.0)],"derivedFrom":[subQ1,subQ0]});Q140=makeQuery(id+"F4.imprint","IMPRINT",FACE,{"disambiguationData":[TD([[makeQuery(id+"F4.imprint","IMPRINT",EDGE,{"disambiguationData":[TD([[subQ2,-1.0]])],"derivedFrom":subQ1}),1.0]])]});}
            var Q141;
            {var subQ0=sQuery(id+"F4.wireOp",EDGE,"E13.41.0");var subQ1=sQuery(id+"F4.wireOp",EDGE,"E11");var subQ2=makeQuery(id+"F4.imprint","INTERSECT",VERTEX,{"disambiguationData":[OD(0.0)],"derivedFrom":[subQ1,subQ0]});Q141=makeQuery(id+"F4.imprint","IMPRINT",FACE,{"disambiguationData":[TD([[makeQuery(id+"F4.imprint","IMPRINT",EDGE,{"disambiguationData":[TD([[subQ2,-1.0]])],"derivedFrom":subQ1}),1.0]])]});}
            var Q142;
            {var subQ0=sQuery(id+"F4.wireOp",EDGE,"E13.42.0");var subQ1=sQuery(id+"F4.wireOp",EDGE,"E11");var subQ2=makeQuery(id+"F4.imprint","INTERSECT",VERTEX,{"disambiguationData":[OD(0.0)],"derivedFrom":[subQ1,subQ0]});Q142=makeQuery(id+"F4.imprint","IMPRINT",FACE,{"disambiguationData":[TD([[makeQuery(id+"F4.imprint","IMPRINT",EDGE,{"disambiguationData":[TD([[subQ2,-1.0]])],"derivedFrom":subQ1}),1.0]])]});}
            var Q143;
            {var subQ0=sQuery(id+"F4.wireOp",EDGE,"E13.43.0");var subQ1=sQuery(id+"F4.wireOp",EDGE,"E11");var subQ2=makeQuery(id+"F4.imprint","INTERSECT",VERTEX,{"disambiguationData":[OD(0.0)],"derivedFrom":[subQ1,subQ0]});Q143=makeQuery(id+"F4.imprint","IMPRINT",FACE,{"disambiguationData":[TD([[makeQuery(id+"F4.imprint","IMPRINT",EDGE,{"disambiguationData":[TD([[subQ2,-1.0]])],"derivedFrom":subQ1}),1.0]])]});}
            var Q144;
            {var subQ0=sQuery(id+"F4.wireOp",EDGE,"E13.44.0");var subQ1=sQuery(id+"F4.wireOp",EDGE,"E11");var subQ2=makeQuery(id+"F4.imprint","INTERSECT",VERTEX,{"disambiguationData":[OD(0.0)],"derivedFrom":[subQ1,subQ0]});Q144=makeQuery(id+"F4.imprint","IMPRINT",FACE,{"disambiguationData":[TD([[makeQuery(id+"F4.imprint","IMPRINT",EDGE,{"disambiguationData":[TD([[subQ2,-1.0]])],"derivedFrom":subQ1}),1.0]])]});}
            var Q145;
            {var subQ0=sQuery(id+"F4.wireOp",EDGE,"E12");var subQ1=sQuery(id+"F4.wireOp",EDGE,"E11");var subQ2=makeQuery(id+"F4.imprint","INTERSECT",VERTEX,{"disambiguationData":[OD(0.0)],"derivedFrom":[subQ1,subQ0]});Q145=makeQuery(id+"F4.imprint","IMPRINT",FACE,{"disambiguationData":[TD([[makeQuery(id+"F4.imprint","IMPRINT",EDGE,{"disambiguationData":[TD([[subQ2,-1.0]])],"derivedFrom":subQ1}),1.0]])]});}
            var Q146;
            {var subQ0=sQuery(id+"F4.wireOp",EDGE,"E13.1.0");var subQ1=sQuery(id+"F4.wireOp",EDGE,"E11");var subQ2=makeQuery(id+"F4.imprint","INTERSECT",VERTEX,{"disambiguationData":[OD(0.0)],"derivedFrom":[subQ1,subQ0]});Q146=makeQuery(id+"F4.imprint","IMPRINT",FACE,{"disambiguationData":[TD([[makeQuery(id+"F4.imprint","IMPRINT",EDGE,{"disambiguationData":[TD([[subQ2,-1.0]])],"derivedFrom":subQ1}),1.0]])]});}
            var Q147;
            {var subQ0=sQuery(id+"F4.wireOp",EDGE,"E13.2.0");var subQ1=sQuery(id+"F4.wireOp",EDGE,"E11");var subQ2=makeQuery(id+"F4.imprint","INTERSECT",VERTEX,{"disambiguationData":[OD(0.0)],"derivedFrom":[subQ1,subQ0]});Q147=makeQuery(id+"F4.imprint","IMPRINT",FACE,{"disambiguationData":[TD([[makeQuery(id+"F4.imprint","IMPRINT",EDGE,{"disambiguationData":[TD([[subQ2,-1.0]])],"derivedFrom":subQ1}),1.0]])]});}
            var Q148;
            {var subQ0=sQuery(id+"F4.wireOp",EDGE,"E13.3.0");var subQ1=sQuery(id+"F4.wireOp",EDGE,"E11");var subQ2=makeQuery(id+"F4.imprint","INTERSECT",VERTEX,{"disambiguationData":[OD(0.0)],"derivedFrom":[subQ1,subQ0]});Q148=makeQuery(id+"F4.imprint","IMPRINT",FACE,{"disambiguationData":[TD([[makeQuery(id+"F4.imprint","IMPRINT",EDGE,{"disambiguationData":[TD([[subQ2,-1.0]])],"derivedFrom":subQ1}),1.0]])]});}
            var Q149;
            {var subQ0=sQuery(id+"F4.wireOp",EDGE,"E13.4.0");var subQ1=sQuery(id+"F4.wireOp",EDGE,"E11");var subQ2=makeQuery(id+"F4.imprint","INTERSECT",VERTEX,{"disambiguationData":[OD(0.0)],"derivedFrom":[subQ1,subQ0]});Q149=makeQuery(id+"F4.imprint","IMPRINT",FACE,{"disambiguationData":[TD([[makeQuery(id+"F4.imprint","IMPRINT",EDGE,{"disambiguationData":[TD([[subQ2,-1.0]])],"derivedFrom":subQ1}),1.0]])]});}
            var Q150;
            {var subQ0=sQuery(id+"F4.wireOp",EDGE,"E13.5.0");var subQ1=sQuery(id+"F4.wireOp",EDGE,"E11");var subQ2=makeQuery(id+"F4.imprint","INTERSECT",VERTEX,{"disambiguationData":[OD(0.0)],"derivedFrom":[subQ1,subQ0]});Q150=makeQuery(id+"F4.imprint","IMPRINT",FACE,{"disambiguationData":[TD([[makeQuery(id+"F4.imprint","IMPRINT",EDGE,{"disambiguationData":[TD([[subQ2,-1.0]])],"derivedFrom":subQ1}),1.0]])]});}
            var Q151;
            {var subQ0=sQuery(id+"F4.wireOp",EDGE,"E13.6.0");var subQ1=sQuery(id+"F4.wireOp",EDGE,"E11");var subQ2=makeQuery(id+"F4.imprint","INTERSECT",VERTEX,{"disambiguationData":[OD(0.0)],"derivedFrom":[subQ1,subQ0]});Q151=makeQuery(id+"F4.imprint","IMPRINT",FACE,{"disambiguationData":[TD([[makeQuery(id+"F4.imprint","IMPRINT",EDGE,{"disambiguationData":[TD([[subQ2,-1.0]])],"derivedFrom":subQ1}),1.0]])]});}
            var Q152;
            {var subQ0=sQuery(id+"F4.wireOp",EDGE,"E13.7.0");var subQ1=sQuery(id+"F4.wireOp",EDGE,"E11");var subQ2=makeQuery(id+"F4.imprint","INTERSECT",VERTEX,{"disambiguationData":[OD(0.0)],"derivedFrom":[subQ1,subQ0]});Q152=makeQuery(id+"F4.imprint","IMPRINT",FACE,{"disambiguationData":[TD([[makeQuery(id+"F4.imprint","IMPRINT",EDGE,{"disambiguationData":[TD([[subQ2,-1.0]])],"derivedFrom":subQ1}),1.0]])]});}
            var Q153;
            {var subQ0=sQuery(id+"F4.wireOp",EDGE,"E13.8.0");var subQ1=sQuery(id+"F4.wireOp",EDGE,"E11");var subQ2=makeQuery(id+"F4.imprint","INTERSECT",VERTEX,{"disambiguationData":[OD(0.0)],"derivedFrom":[subQ1,subQ0]});Q153=makeQuery(id+"F4.imprint","IMPRINT",FACE,{"disambiguationData":[TD([[makeQuery(id+"F4.imprint","IMPRINT",EDGE,{"disambiguationData":[TD([[subQ2,-1.0]])],"derivedFrom":subQ1}),1.0]])]});}
            var Q154;
            {var subQ0=sQuery(id+"F4.wireOp",EDGE,"E13.9.0");var subQ1=sQuery(id+"F4.wireOp",EDGE,"E11");var subQ2=makeQuery(id+"F4.imprint","INTERSECT",VERTEX,{"disambiguationData":[OD(0.0)],"derivedFrom":[subQ1,subQ0]});Q154=makeQuery(id+"F4.imprint","IMPRINT",FACE,{"disambiguationData":[TD([[makeQuery(id+"F4.imprint","IMPRINT",EDGE,{"disambiguationData":[TD([[subQ2,-1.0]])],"derivedFrom":subQ1}),1.0]])]});}
            var Q155;
            {var subQ0=sQuery(id+"F4.wireOp",EDGE,"E13.10.0");var subQ1=sQuery(id+"F4.wireOp",EDGE,"E11");var subQ2=makeQuery(id+"F4.imprint","INTERSECT",VERTEX,{"disambiguationData":[OD(0.0)],"derivedFrom":[subQ1,subQ0]});Q155=makeQuery(id+"F4.imprint","IMPRINT",FACE,{"disambiguationData":[TD([[makeQuery(id+"F4.imprint","IMPRINT",EDGE,{"disambiguationData":[TD([[subQ2,-1.0]])],"derivedFrom":subQ1}),1.0]])]});}
            var Q156;
            {var subQ0=sQuery(id+"F4.wireOp",EDGE,"E13.11.0");var subQ1=sQuery(id+"F4.wireOp",EDGE,"E11");var subQ2=makeQuery(id+"F4.imprint","INTERSECT",VERTEX,{"disambiguationData":[OD(0.0)],"derivedFrom":[subQ1,subQ0]});Q156=makeQuery(id+"F4.imprint","IMPRINT",FACE,{"disambiguationData":[TD([[makeQuery(id+"F4.imprint","IMPRINT",EDGE,{"disambiguationData":[TD([[subQ2,-1.0]])],"derivedFrom":subQ1}),1.0]])]});}
            var Q157;
            {var subQ0=sQuery(id+"F4.wireOp",EDGE,"E13.12.0");var subQ1=sQuery(id+"F4.wireOp",EDGE,"E11");var subQ2=makeQuery(id+"F4.imprint","INTERSECT",VERTEX,{"disambiguationData":[OD(0.0)],"derivedFrom":[subQ1,subQ0]});Q157=makeQuery(id+"F4.imprint","IMPRINT",FACE,{"disambiguationData":[TD([[makeQuery(id+"F4.imprint","IMPRINT",EDGE,{"disambiguationData":[TD([[subQ2,-1.0]])],"derivedFrom":subQ1}),1.0]])]});}
            var Q158;
            {var subQ0=sQuery(id+"F4.wireOp",EDGE,"E13.13.0");var subQ1=sQuery(id+"F4.wireOp",EDGE,"E11");var subQ2=makeQuery(id+"F4.imprint","INTERSECT",VERTEX,{"disambiguationData":[OD(0.0)],"derivedFrom":[subQ1,subQ0]});Q158=makeQuery(id+"F4.imprint","IMPRINT",FACE,{"disambiguationData":[TD([[makeQuery(id+"F4.imprint","IMPRINT",EDGE,{"disambiguationData":[TD([[subQ2,-1.0]])],"derivedFrom":subQ1}),1.0]])]});}
            var Q159;
            {var subQ0=sQuery(id+"F4.wireOp",EDGE,"E13.14.0");var subQ1=sQuery(id+"F4.wireOp",EDGE,"E11");var subQ2=makeQuery(id+"F4.imprint","INTERSECT",VERTEX,{"disambiguationData":[OD(0.0)],"derivedFrom":[subQ1,subQ0]});Q159=makeQuery(id+"F4.imprint","IMPRINT",FACE,{"disambiguationData":[TD([[makeQuery(id+"F4.imprint","IMPRINT",EDGE,{"disambiguationData":[TD([[subQ2,-1.0]])],"derivedFrom":subQ1}),1.0]])]});}
            var Q160;
            {var subQ0=sQuery(id+"F4.wireOp",EDGE,"E13.15.0");var subQ1=sQuery(id+"F4.wireOp",EDGE,"E11");var subQ2=makeQuery(id+"F4.imprint","INTERSECT",VERTEX,{"disambiguationData":[OD(0.0)],"derivedFrom":[subQ1,subQ0]});Q160=makeQuery(id+"F4.imprint","IMPRINT",FACE,{"disambiguationData":[TD([[makeQuery(id+"F4.imprint","IMPRINT",EDGE,{"disambiguationData":[TD([[subQ2,-1.0]])],"derivedFrom":subQ1}),1.0]])]});}
            var Q161;
            {var subQ0=sQuery(id+"F4.wireOp",EDGE,"E13.16.0");var subQ1=sQuery(id+"F4.wireOp",EDGE,"E11");var subQ2=makeQuery(id+"F4.imprint","INTERSECT",VERTEX,{"disambiguationData":[OD(0.0)],"derivedFrom":[subQ1,subQ0]});Q161=makeQuery(id+"F4.imprint","IMPRINT",FACE,{"disambiguationData":[TD([[makeQuery(id+"F4.imprint","IMPRINT",EDGE,{"disambiguationData":[TD([[subQ2,-1.0]])],"derivedFrom":subQ1}),1.0]])]});}
            var Q162;
            {var subQ0=sQuery(id+"F4.wireOp",EDGE,"E13.17.0");var subQ1=sQuery(id+"F4.wireOp",EDGE,"E11");var subQ2=makeQuery(id+"F4.imprint","INTERSECT",VERTEX,{"disambiguationData":[OD(0.0)],"derivedFrom":[subQ1,subQ0]});Q162=makeQuery(id+"F4.imprint","IMPRINT",FACE,{"disambiguationData":[TD([[makeQuery(id+"F4.imprint","IMPRINT",EDGE,{"disambiguationData":[TD([[subQ2,-1.0]])],"derivedFrom":subQ1}),1.0]])]});}
            var Q163;
            {var subQ0=sQuery(id+"F4.wireOp",EDGE,"E13.18.0");var subQ1=sQuery(id+"F4.wireOp",EDGE,"E11");var subQ2=makeQuery(id+"F4.imprint","INTERSECT",VERTEX,{"disambiguationData":[OD(0.0)],"derivedFrom":[subQ1,subQ0]});Q163=makeQuery(id+"F4.imprint","IMPRINT",FACE,{"disambiguationData":[TD([[makeQuery(id+"F4.imprint","IMPRINT",EDGE,{"disambiguationData":[TD([[subQ2,-1.0]])],"derivedFrom":subQ1}),1.0]])]});}
            var Q164;
            {var subQ0=sQuery(id+"F4.wireOp",EDGE,"E13.19.0");var subQ1=sQuery(id+"F4.wireOp",EDGE,"E11");var subQ2=makeQuery(id+"F4.imprint","INTERSECT",VERTEX,{"disambiguationData":[OD(0.0)],"derivedFrom":[subQ1,subQ0]});Q164=makeQuery(id+"F4.imprint","IMPRINT",FACE,{"disambiguationData":[TD([[makeQuery(id+"F4.imprint","IMPRINT",EDGE,{"disambiguationData":[TD([[subQ2,-1.0]])],"derivedFrom":subQ1}),1.0]])]});}
            var Q165;
            {var subQ0=sQuery(id+"F4.wireOp",EDGE,"E13.20.0");var subQ1=sQuery(id+"F4.wireOp",EDGE,"E11");var subQ2=makeQuery(id+"F4.imprint","INTERSECT",VERTEX,{"disambiguationData":[OD(0.0)],"derivedFrom":[subQ1,subQ0]});Q165=makeQuery(id+"F4.imprint","IMPRINT",FACE,{"disambiguationData":[TD([[makeQuery(id+"F4.imprint","IMPRINT",EDGE,{"disambiguationData":[TD([[subQ2,-1.0]])],"derivedFrom":subQ1}),1.0]])]});}
            var Q166;
            {var subQ0=sQuery(id+"F4.wireOp",EDGE,"E13.21.0");var subQ1=sQuery(id+"F4.wireOp",EDGE,"E11");var subQ2=makeQuery(id+"F4.imprint","INTERSECT",VERTEX,{"disambiguationData":[OD(0.0)],"derivedFrom":[subQ1,subQ0]});Q166=makeQuery(id+"F4.imprint","IMPRINT",FACE,{"disambiguationData":[TD([[makeQuery(id+"F4.imprint","IMPRINT",EDGE,{"disambiguationData":[TD([[subQ2,-1.0]])],"derivedFrom":subQ1}),1.0]])]});}
            var Q167;
            {var subQ0=sQuery(id+"F4.wireOp",EDGE,"E13.22.0");var subQ1=sQuery(id+"F4.wireOp",EDGE,"E11");var subQ2=makeQuery(id+"F4.imprint","INTERSECT",VERTEX,{"disambiguationData":[OD(0.0)],"derivedFrom":[subQ1,subQ0]});Q167=makeQuery(id+"F4.imprint","IMPRINT",FACE,{"disambiguationData":[TD([[makeQuery(id+"F4.imprint","IMPRINT",EDGE,{"disambiguationData":[TD([[subQ2,-1.0]])],"derivedFrom":subQ1}),1.0]])]});}
            var Q168;
            {var subQ0=sQuery(id+"F4.wireOp",EDGE,"E13.23.0");var subQ1=sQuery(id+"F4.wireOp",EDGE,"E11");var subQ2=makeQuery(id+"F4.imprint","INTERSECT",VERTEX,{"disambiguationData":[OD(0.0)],"derivedFrom":[subQ1,subQ0]});Q168=makeQuery(id+"F4.imprint","IMPRINT",FACE,{"disambiguationData":[TD([[makeQuery(id+"F4.imprint","IMPRINT",EDGE,{"disambiguationData":[TD([[subQ2,-1.0]])],"derivedFrom":subQ1}),1.0]])]});}
            var Q169;
            {var subQ0=sQuery(id+"F4.wireOp",EDGE,"E13.24.0");var subQ1=sQuery(id+"F4.wireOp",EDGE,"E11");var subQ2=makeQuery(id+"F4.imprint","INTERSECT",VERTEX,{"disambiguationData":[OD(0.0)],"derivedFrom":[subQ1,subQ0]});Q169=makeQuery(id+"F4.imprint","IMPRINT",FACE,{"disambiguationData":[TD([[makeQuery(id+"F4.imprint","IMPRINT",EDGE,{"disambiguationData":[TD([[subQ2,-1.0]])],"derivedFrom":subQ1}),1.0]])]});}
            var Q170;
            {var subQ0=sQuery(id+"F4.wireOp",EDGE,"E13.25.0");var subQ1=sQuery(id+"F4.wireOp",EDGE,"E11");var subQ2=makeQuery(id+"F4.imprint","INTERSECT",VERTEX,{"disambiguationData":[OD(0.0)],"derivedFrom":[subQ1,subQ0]});Q170=makeQuery(id+"F4.imprint","IMPRINT",FACE,{"disambiguationData":[TD([[makeQuery(id+"F4.imprint","IMPRINT",EDGE,{"disambiguationData":[TD([[subQ2,-1.0]])],"derivedFrom":subQ1}),1.0]])]});}
            var Q171;
            {var subQ0=sQuery(id+"F4.wireOp",EDGE,"E13.26.0");var subQ1=sQuery(id+"F4.wireOp",EDGE,"E11");var subQ2=makeQuery(id+"F4.imprint","INTERSECT",VERTEX,{"disambiguationData":[OD(0.0)],"derivedFrom":[subQ1,subQ0]});Q171=makeQuery(id+"F4.imprint","IMPRINT",FACE,{"disambiguationData":[TD([[makeQuery(id+"F4.imprint","IMPRINT",EDGE,{"disambiguationData":[TD([[subQ2,-1.0]])],"derivedFrom":subQ1}),1.0]])]});}
            var Q172;
            {var subQ0=sQuery(id+"F4.wireOp",EDGE,"E13.27.0");var subQ1=sQuery(id+"F4.wireOp",EDGE,"E11");var subQ2=makeQuery(id+"F4.imprint","INTERSECT",VERTEX,{"disambiguationData":[OD(0.0)],"derivedFrom":[subQ1,subQ0]});Q172=makeQuery(id+"F4.imprint","IMPRINT",FACE,{"disambiguationData":[TD([[makeQuery(id+"F4.imprint","IMPRINT",EDGE,{"disambiguationData":[TD([[subQ2,-1.0]])],"derivedFrom":subQ1}),1.0]])]});}
            var Q173;
            {var subQ0=sQuery(id+"F4.wireOp",EDGE,"E13.28.0");var subQ1=sQuery(id+"F4.wireOp",EDGE,"E11");var subQ2=makeQuery(id+"F4.imprint","INTERSECT",VERTEX,{"disambiguationData":[OD(0.0)],"derivedFrom":[subQ1,subQ0]});Q173=makeQuery(id+"F4.imprint","IMPRINT",FACE,{"disambiguationData":[TD([[makeQuery(id+"F4.imprint","IMPRINT",EDGE,{"disambiguationData":[TD([[subQ2,-1.0]])],"derivedFrom":subQ1}),1.0]])]});}
            var Q174;
            {var subQ0=sQuery(id+"F4.wireOp",EDGE,"E13.29.0");var subQ1=sQuery(id+"F4.wireOp",EDGE,"E11");var subQ2=makeQuery(id+"F4.imprint","INTERSECT",VERTEX,{"disambiguationData":[OD(0.0)],"derivedFrom":[subQ1,subQ0]});Q174=makeQuery(id+"F4.imprint","IMPRINT",FACE,{"disambiguationData":[TD([[makeQuery(id+"F4.imprint","IMPRINT",EDGE,{"disambiguationData":[TD([[subQ2,-1.0]])],"derivedFrom":subQ1}),1.0]])]});}
            var Q175;
            {var subQ0=sQuery(id+"F4.wireOp",EDGE,"E13.30.0");var subQ1=sQuery(id+"F4.wireOp",EDGE,"E11");var subQ2=makeQuery(id+"F4.imprint","INTERSECT",VERTEX,{"disambiguationData":[OD(0.0)],"derivedFrom":[subQ1,subQ0]});Q175=makeQuery(id+"F4.imprint","IMPRINT",FACE,{"disambiguationData":[TD([[makeQuery(id+"F4.imprint","IMPRINT",EDGE,{"disambiguationData":[TD([[subQ2,-1.0]])],"derivedFrom":subQ1}),1.0]])]});}
            var Q176;
            {var subQ0=sQuery(id+"F4.wireOp",EDGE,"E13.31.0");var subQ1=sQuery(id+"F4.wireOp",EDGE,"E11");var subQ2=makeQuery(id+"F4.imprint","INTERSECT",VERTEX,{"disambiguationData":[OD(0.0)],"derivedFrom":[subQ1,subQ0]});Q176=makeQuery(id+"F4.imprint","IMPRINT",FACE,{"disambiguationData":[TD([[makeQuery(id+"F4.imprint","IMPRINT",EDGE,{"disambiguationData":[TD([[subQ2,-1.0]])],"derivedFrom":subQ1}),1.0]])]});}
            var Q177;
            {var subQ0=sQuery(id+"F4.wireOp",EDGE,"E13.32.0");var subQ1=sQuery(id+"F4.wireOp",EDGE,"E11");var subQ2=makeQuery(id+"F4.imprint","INTERSECT",VERTEX,{"disambiguationData":[OD(0.0)],"derivedFrom":[subQ1,subQ0]});Q177=makeQuery(id+"F4.imprint","IMPRINT",FACE,{"disambiguationData":[TD([[makeQuery(id+"F4.imprint","IMPRINT",EDGE,{"disambiguationData":[TD([[subQ2,-1.0]])],"derivedFrom":subQ1}),1.0]])]});}
            var Q178;
            {var subQ0=sQuery(id+"F4.wireOp",EDGE,"E13.33.0");var subQ1=sQuery(id+"F4.wireOp",EDGE,"E11");var subQ2=makeQuery(id+"F4.imprint","INTERSECT",VERTEX,{"disambiguationData":[OD(0.0)],"derivedFrom":[subQ1,subQ0]});Q178=makeQuery(id+"F4.imprint","IMPRINT",FACE,{"disambiguationData":[TD([[makeQuery(id+"F4.imprint","IMPRINT",EDGE,{"disambiguationData":[TD([[subQ2,-1.0]])],"derivedFrom":subQ1}),1.0]])]});}
            var Q179;
            {var subQ0=sQuery(id+"F4.wireOp",EDGE,"E13.34.0");var subQ1=sQuery(id+"F4.wireOp",EDGE,"E11");var subQ2=makeQuery(id+"F4.imprint","INTERSECT",VERTEX,{"disambiguationData":[OD(0.0)],"derivedFrom":[subQ1,subQ0]});Q179=makeQuery(id+"F4.imprint","IMPRINT",FACE,{"disambiguationData":[TD([[makeQuery(id+"F4.imprint","IMPRINT",EDGE,{"disambiguationData":[TD([[subQ2,1.0]])],"derivedFrom":subQ1}),1.0]])]});}
            extrude(context, id + "F5", {"entities" : qUnion([Q0, Q1, Q2, Q3, Q4, Q5, Q6, Q7, Q8, Q9, Q10, Q11, Q12, Q13, Q14, Q15, Q16, Q17, Q18, Q19, Q20, Q21, Q22, Q23, Q24, Q25, Q26, Q27, Q28, Q29, Q30, Q31, Q32, Q33, Q34, Q35, Q36, Q37, Q38, Q39, Q40, Q41, Q42, Q43, Q44, Q45, Q46, Q47, Q48, Q49, Q50, Q51, Q52, Q53, Q54, Q55, Q56, Q57, Q58, Q59, Q60, Q61, Q62, Q63, Q64, Q65, Q66, Q67, Q68, Q69, Q70, Q71, Q72, Q73, Q74, Q75, Q76, Q77, Q78, Q79, Q80, Q81, Q82, Q83, Q84, Q85, Q86, Q87, Q88, Q89, Q90, Q91, Q92, Q93, Q94, Q95, Q96, Q97, Q98, Q99, Q100, Q101, Q102, Q103, Q104, Q105, Q106, Q107, Q108, Q109, Q110, Q111, Q112, Q113, Q114, Q115, Q116, Q117, Q118, Q119, Q120, Q121, Q122, Q123, Q124, Q125, Q126, Q127, Q128, Q129, Q130, Q131, Q132, Q133, Q134, Q135, Q136, Q137, Q138, Q139, Q140, Q141, Q142, Q143, Q144, Q145, Q146, Q147, Q148, Q149, Q150, Q151, Q152, Q153, Q154, Q155, Q156, Q157, Q158, Q159, Q160, Q161, Q162, Q163, Q164, Q165, Q166, Q167, Q168, Q169, Q170, Q171, Q172, Q173, Q174, Q175, Q176, Q177, Q178, Q179]), "operationType" : NewBodyOperationType.REMOVE, "oppositeDirection" : true, "depth" : 7 * mm, "offsetDistance" : 25 * mm});
        }
    });
